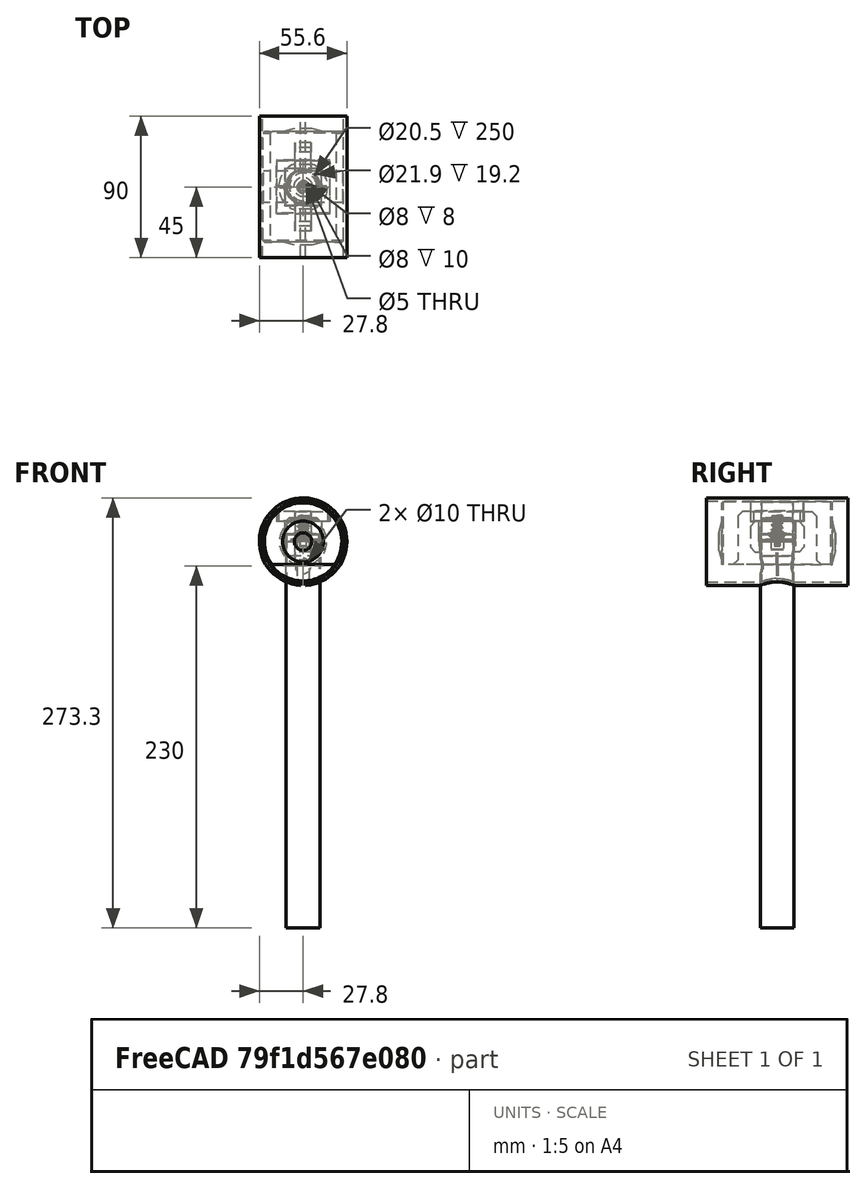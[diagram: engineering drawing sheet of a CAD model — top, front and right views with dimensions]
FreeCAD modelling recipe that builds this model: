
FCSTD DOCUMENT  (FreeCAD 1.0R39109 (Git))
Label: HammerV2
License: All rights reserved
LicenseURL: https://en.wikipedia.org/wiki/All_rights_reserved
objects: TechDraw::DrawViewDimension×61, TechDraw::DrawProjGroupItem×26, Part::Feature×23, Sketcher::SketchObject×22, App::DocumentObjectGroupPython×19, App::FeaturePython×16, App::Link×14, PartDesign::Body×11, TechDraw::DrawViewBalloon×11, PartDesign::Pad×10, PartDesign::Pocket×9, TechDraw::DrawSVGTemplate×9, TechDraw::DrawPage×9, TechDraw::DrawViewAnnotation×8, TechDraw::DrawProjGroup×8, PartDesign::Chamfer×5, App::DocumentObjectGroup×4, PartDesign::PolarPattern×3, PartDesign::Mirrored×3, PartDesign::AdditiveHelix×3, +9 more types
note: 282 computed .brp shape members not serialized (recipe doc carries the construction recipe); baked Part::Feature solids carry a one-line shape summary decoded from their .brp

FEATURE [Sketcher::SketchObject] Sketch011
  ArcFitTolerance = 1e-06
  AttachmentSupport = -> [XY_Plane009]
  FullyConstrained = true
  MakeInternals = false
  MapMode = 5
  sketch-geometry (5):
    g0: LineSegment StartX=-11.55 StartY=-11.55 StartZ=0 EndX=11.55 EndY=-11.55 EndZ=0
    g1: LineSegment StartX=11.55 StartY=-11.55 StartZ=0 EndX=11.55 EndY=11.55 EndZ=0
    g2: LineSegment StartX=11.55 StartY=11.55 StartZ=0 EndX=-11.55 EndY=11.55 EndZ=0
    g3: LineSegment StartX=-11.55 StartY=11.55 StartZ=0 EndX=-11.55 EndY=-11.55 EndZ=0
    g4: GeomPoint [constr] X=0 Y=0 Z=0
  constraints (12):
    c: Coincident(g0,g1)
    c: Coincident(g1,g2)
    c: Coincident(g2,g3)
    c: Coincident(g3,g0)
    c: Horizontal(g0)
    c: Horizontal(g2)
    c: Vertical(g1)
    c: Vertical(g3)
    c: Symmetric(g2,g0,g4)
    c: Coincident(g4,g-1)
    c: DistanceX(g2,g2) = 23.1
    c: Equal(g1,g2)
FEATURE [PartDesign::Pad] Pad007
  Direction = (0,0,1)
  Length = 5
  Length2 = 10
  Profile = -> Sketch011
  ReferenceAxis = -> Sketch011 [N_Axis]
  Refine = true
  Suppressed = false
  Type = 0
FEATURE [Sketcher::SketchObject] Sketch012
  ArcFitTolerance = 1e-06
  AttachmentSupport = -> [XY_Plane009]
  FullyConstrained = true
  MakeInternals = false
  MapMode = 5
  expr: Constraints[16] = 23.1 / 2
  sketch-geometry (6):
    g0: LineSegment StartX=0 StartY=11.55 StartZ=0 EndX=1.8 EndY=11.55 EndZ=0
    g1: LineSegment StartX=1.8 StartY=11.55 StartZ=0 EndX=1.8 EndY=1.8 EndZ=0
    g2: LineSegment StartX=1.8 StartY=1.8 StartZ=0 EndX=11.55 EndY=1.8 EndZ=0
    g3: LineSegment StartX=11.55 StartY=1.8 StartZ=0 EndX=11.55 EndY=0 EndZ=0
    g4: LineSegment StartX=0 StartY=11.55 StartZ=0 EndX=0 EndY=0 EndZ=0
    g5: LineSegment StartX=0 StartY=0 StartZ=0 EndX=11.55 EndY=0 EndZ=0
  constraints (17):
    c: Horizontal(g0)
    c: Coincident(g0,g1)
    c: Vertical(g1)
    c: Coincident(g1,g2)
    c: Horizontal(g2)
    c: Coincident(g2,g3)
    c: Vertical(g3)
    c: Coincident(g4,g0)
    c: Vertical(g4)
    c: Coincident(g5,g4)
    c: Coincident(g5,g3)
    c: Horizontal(g5)
    c: Coincident(g4,g-1)
    c: DistanceX(g0,g0) = 1.8
    c: Equal(g3,g0)
    c: Equal(g4,g5)
    c: DistanceY(g4,g4) = 11.55
FEATURE [PartDesign::Pad] Pad008
  BaseFeature = -> Pad007
  Direction = (0,0,1)
  Length = 2.8
  Length2 = 10
  Profile = -> Sketch012
  ReferenceAxis = -> Sketch012 [N_Axis]
  Refine = true
  Reversed = true
  Suppressed = false
  Type = 0
FEATURE [PartDesign::PolarPattern] PolarPattern001
  Angle = 360
  Axis = -> Sketch012 [N_Axis]
  BaseFeature = -> Pad008
  Mode = 0
  Occurrences = 4
  Offset = 120
  Originals = -> [Pad008]
  Refine = true
  Suppressed = false
  TransformMode = 0
FEATURE [Sketcher::SketchObject] Sketch013
  ArcFitTolerance = 1e-06
  AttachmentSupport = -> [XY_Plane009]
  FullyConstrained = true
  MakeInternals = false
  MapMode = 5
  sketch-geometry (1):
    g0: Circle CenterX=0 CenterY=0 CenterZ=0 NormalX=0 NormalY=0 NormalZ=1 AngleXU=0 Radius=10.5
  constraints (2):
    c: Coincident(g0,g-1)
    c: Diameter(g0) = 21
FEATURE [PartDesign::Pad] Pad009
  BaseFeature = -> PolarPattern001
  Direction = (0,0,1)
  Length = 9
  Length2 = 10
  Profile = -> Sketch013
  ReferenceAxis = -> Sketch013 [N_Axis]
  Refine = true
  Reversed = true
  Suppressed = false
  TaperAngle = -2
  Type = 0
FEATURE [Sketcher::SketchObject] Sketch014
  ArcFitTolerance = 1e-06
  AttachmentOffset = pos=(0,0,-5) rot=(0,0,1;0rad)
  AttachmentSupport = -> [XY_Plane009]
  FullyConstrained = true
  MakeInternals = false
  MapMode = 5
  Placement = pos=(0,0,-5) rot=(0,0,1;0rad)
  sketch-geometry (1):
    g0: Circle CenterX=0 CenterY=0 CenterZ=0 NormalX=0 NormalY=0 NormalZ=1 AngleXU=0 Radius=4
  constraints (2):
    c: Diameter(g0) = 8
    c: Coincident(g0,g-1)
FEATURE [PartDesign::Pocket] Pocket003
  BaseFeature = -> Pad009
  Direction = (0,0,-1)
  Length = 0
  Length2 = 5
  Profile = -> Sketch014
  ReferenceAxis = -> Sketch014 [N_Axis]
  Refine = true
  Suppressed = false
  Type = 3
  UpToFace = -> Pad009 [Face11]
FEATURE [PartDesign::Chamfer] Chamfer003
  Angle = 45
  Base = -> Pocket003 [Edge6,Edge11,Edge39,Edge37]
  BaseFeature = -> Pocket003
  ChamferType = 0
  FlipDirection = false
  Refine = true
  Size = 1
  Size2 = 1
  SupportTransform = false
  Suppressed = false
  UseAllEdges = false
FEATURE [Sketcher::SketchObject] Sketch015
  ArcFitTolerance = 1e-06
  AttachmentSupport = -> [XZ_Plane010]
  FullyConstrained = true
  MakeInternals = false
  MapMode = 5
  Placement = pos=(0,0,0) rot=(1,0,0;1.5708rad)
  expr: Constraints[13] = 5 / 2
  sketch-geometry (6):
    g0: LineSegment StartX=-4e-16 StartY=0 StartZ=0 EndX=2.5 EndY=0 EndZ=0
    g1: LineSegment StartX=2.5 StartY=0 StartZ=0 EndX=2.5 EndY=2.8 EndZ=0
    g2: LineSegment StartX=2.5 StartY=2.8 StartZ=0 EndX=4 EndY=2.8 EndZ=0
    g3: LineSegment StartX=4 StartY=2.8 StartZ=0 EndX=4 EndY=4 EndZ=0
    g4: LineSegment StartX=4 StartY=4 StartZ=0 EndX=0 EndY=4 EndZ=0
    g5: LineSegment StartX=0 StartY=4 StartZ=0 EndX=-4e-16 EndY=0 EndZ=0
  constraints (17):
    c: Coincident(g-1,g0)
    c: PointOnObject(g0,g-1)
    c: Coincident(g0,g1)
    c: Vertical(g1)
    c: Coincident(g1,g2)
    c: Horizontal(g2)
    c: Coincident(g2,g3)
    c: Vertical(g3)
    c: Coincident(g3,g4)
    c: PointOnObject(g4,g-2)
    c: Horizontal(g4)
    c: Coincident(g4,g5)
    c: Coincident(g5,g0)
    c: DistanceX(g0,g0) = 2.5
    c: DistanceX(g4,g4) = 4
    c: DistanceY(g3,g3) = 1.2
    c: DistanceY(g5,g5) = 4
FEATURE [PartDesign::Revolution] Revolution
  Angle = 360
  Angle2 = 60
  Axis = (0,2e-16,1)
  Base = (0,0,0)
  Placement = pos=(0,0,0) rot=(1,0,0;1.5708rad)
  Profile = -> Sketch015
  ReferenceAxis = -> Sketch015 [V_Axis]
  Refine = true
  Reversed = true
  Suppressed = false
  Type = 0
FEATURE [PartDesign::Chamfer] Chamfer002
  Angle = 45
  Base = -> Revolution [Edge1]
  BaseFeature = -> Revolution
  ChamferType = 0
  FlipDirection = false
  Placement = pos=(0,0,0) rot=(1,0,0;1.5708rad)
  Refine = true
  Size = 0.5
  Size2 = 1
  SupportTransform = false
  Suppressed = false
  UseAllEdges = false
FEATURE [PartDesign::Body] Body008  label="Spring_Top"
  AllowCompound = false
  Group = -> [Sketch015,Revolution,Chamfer002]
  Origin = -> Origin010
  Tip = -> Chamfer002
FEATURE [Sketcher::SketchObject] Sketch016
  ArcFitTolerance = 1e-06
  AttachmentSupport = -> [XZ_Plane011]
  FullyConstrained = false
  MakeInternals = false
  MapMode = 5
  Placement = pos=(0,0,0) rot=(1,0,0;1.5708rad)
  expr: Constraints[5] = <<HMRProperties>>.head_diameter
  expr: Constraints[9] = <<HMRProperties>>.head_cutoff
  sketch-geometry (4):
    g0: GeomPoint [constr] X=0 Y=-25.6 Z=0
    g1: ArcOfCircle CenterX=0 CenterY=0 CenterZ=0 NormalX=0 NormalY=0 NormalZ=1 AngleXU=0 Radius=25.6 StartAngle=5.6763 EndAngle=10.0317
    g2: LineSegment StartX=21.0286 StartY=-14.6 StartZ=0 EndX=-21.0286 EndY=-14.6 EndZ=0
    g3: ArcOfCircle [constr] CenterX=0 CenterY=0 CenterZ=0 NormalX=0 NormalY=0 NormalZ=1 AngleXU=0 Radius=25.6 StartAngle=3.89407 EndAngle=5.6763
  constraints (10):
    c: PointOnObject(g0,g-2)
    c: Coincident(g1,g-1)
    c: Coincident(g2,g1)
    c: Coincident(g2,g1)
    c: Horizontal(g2)
    c: Diameter(g1) = 51.2
    c: Coincident(g3,g1)
    c: Coincident(g3,g1)
    c: PointOnObject(g0,g3)
    c: DistanceY(g0,g1) = 11
FEATURE [PartDesign::Pad] Pad010
  Direction = (0,-1,2e-16)
  Length = 70
  Length2 = 10
  Midplane = true
  Placement = pos=(0,0,0) rot=(1,0,0;1.5708rad)
  Profile = -> Sketch016
  ReferenceAxis = -> Sketch016 [N_Axis]
  Refine = true
  Suppressed = false
  Type = 0
  expr: Length = <<HMRProperties>>.head_length
FEATURE [Sketcher::SketchObject] Sketch017
  ArcFitTolerance = 1e-06
  AttachmentOffset = pos=(0,0,25.6) rot=(0,0,1;0rad)
  AttachmentSupport = -> [XY_Plane011]
  FullyConstrained = true
  MakeInternals = false
  MapMode = 5
  Placement = pos=(0,0,25.6) rot=(0,0,1;0rad)
  expr: .AttachmentOffset.Base.z = <<HMRProperties>>.head_diameter / 2
  expr: Constraints[9] = <<HMRProperties>>.top_sensor_pocket_size
  sketch-geometry (5):
    g0: LineSegment StartX=-17 StartY=-17 StartZ=0 EndX=17 EndY=-17 EndZ=0
    g1: LineSegment StartX=17 StartY=-17 StartZ=0 EndX=17 EndY=17 EndZ=0
    g2: LineSegment StartX=17 StartY=17 StartZ=0 EndX=-17 EndY=17 EndZ=0
    g3: LineSegment StartX=-17 StartY=17 StartZ=0 EndX=-17 EndY=-17 EndZ=0
    g4: GeomPoint [constr] X=0 Y=0 Z=0
  constraints (12):
    c: Coincident(g0,g1)
    c: Coincident(g1,g2)
    c: Coincident(g2,g3)
    c: Coincident(g3,g0)
    c: Horizontal(g0)
    c: Horizontal(g2)
    c: Vertical(g1)
    c: Vertical(g3)
    c: Symmetric(g2,g0,g4)
    c: Distance(g0,g2) = 34
    c: Coincident(g4,g-1)
    c: Equal(g0,g3)
FEATURE [PartDesign::Pocket] Pocket004
  BaseFeature = -> Pad010
  Direction = (0,0,-1)
  Length = 13
  Length2 = 5
  Placement = pos=(0,0,0) rot=(1,0,0;1.5708rad)
  Profile = -> Sketch017
  ReferenceAxis = -> Sketch017 [N_Axis]
  Refine = true
  Suppressed = false
  Type = 0
  expr: Length = <<HMRProperties>>.top_sensor_pocket_depth
FEATURE [Sketcher::SketchObject] Sketch018
  ArcFitTolerance = 1e-06
  AttachmentOffset = pos=(0,0,12.6) rot=(0,0,1;0rad)
  AttachmentSupport = -> [XY_Plane011]
  FullyConstrained = true
  MakeInternals = false
  MapMode = 5
  Placement = pos=(0,0,12.6) rot=(0,0,1;0rad)
  expr: .AttachmentOffset.Base.z = <<HMRProperties>>.head_diameter / 2 - <<HMRProperties>>.top_sensor_pocket_depth
  expr: Constraints[11] = <<HMRProperties>>.pusher_pocket_size
  sketch-geometry (5):
    g0: LineSegment StartX=-11.75 StartY=-11.75 StartZ=0 EndX=11.75 EndY=-11.75 EndZ=0
    g1: LineSegment StartX=11.75 StartY=-11.75 StartZ=0 EndX=11.75 EndY=11.75 EndZ=0
    g2: LineSegment StartX=11.75 StartY=11.75 StartZ=0 EndX=-11.75 EndY=11.75 EndZ=0
    g3: LineSegment StartX=-11.75 StartY=11.75 StartZ=0 EndX=-11.75 EndY=-11.75 EndZ=0
    g4: GeomPoint [constr] X=0 Y=0 Z=0
  constraints (12):
    c: Coincident(g0,g1)
    c: Coincident(g1,g2)
    c: Coincident(g2,g3)
    c: Coincident(g3,g0)
    c: Horizontal(g0)
    c: Horizontal(g2)
    c: Vertical(g1)
    c: Vertical(g3)
    c: Symmetric(g2,g0,g4)
    c: Coincident(g4,g-1)
    c: Equal(g2,g1)
    c: DistanceX(g2,g2) = 23.5
FEATURE [PartDesign::Pocket] Pocket005
  BaseFeature = -> Pocket004
  Direction = (0,0,-1)
  Length = 8
  Length2 = 5
  Placement = pos=(0,0,0) rot=(1,0,0;1.5708rad)
  Profile = -> Sketch018
  ReferenceAxis = -> Sketch018 [N_Axis]
  Refine = true
  Suppressed = false
  Type = 0
  expr: Length = <<HMRProperties>>.pusher_pocket_depth
FEATURE [Sketcher::SketchObject] Sketch019
  ArcFitTolerance = 1e-06
  AttachmentOffset = pos=(0,0,25.6) rot=(0,0,1;0rad)
  AttachmentSupport = -> [XY_Plane011]
  FullyConstrained = true
  MakeInternals = false
  MapMode = 5
  Placement = pos=(0,0,25.6) rot=(0,0,1;0rad)
  expr: .AttachmentOffset.Base.z = <<HMRProperties>>.head_diameter / 2
  expr: Constraints[1] = <<HMRProperties>>.handle_hole_diameter
  sketch-geometry (1):
    g0: Circle CenterX=0 CenterY=0 CenterZ=0 NormalX=0 NormalY=0 NormalZ=1 AngleXU=0 Radius=10.95
  constraints (2):
    c: Coincident(g0,g-1)
    c: Diameter(g0) = 21.9
FEATURE [PartDesign::Pocket] Pocket006
  BaseFeature = -> Pocket005
  Direction = (0,0,-1)
  Length = 5
  Length2 = 5
  Placement = pos=(0,0,0) rot=(1,0,0;1.5708rad)
  Profile = -> Sketch019
  ReferenceAxis = -> Sketch019 [N_Axis]
  Refine = true
  Suppressed = false
  Type = 1
FEATURE [Sketcher::SketchObject] Sketch020
  ArcFitTolerance = 1e-06
  AttachmentOffset = pos=(0,0,4.6) rot=(0,0,1;0rad)
  AttachmentSupport = -> [XY_Plane011]
  FullyConstrained = true
  MakeInternals = false
  MapMode = 5
  Placement = pos=(0,0,4.6) rot=(0,0,1;0rad)
  expr: .AttachmentOffset.Base.z = <<HMRProperties>>.head_diameter / 2 - <<HMRProperties>>.top_sensor_pocket_depth - <<HMRProperties>>.pusher_pocket_depth
  expr: Constraints[16] = <<HMRProperties>>.pusher_pocket_size / 2
  sketch-geometry (6):
    g0: LineSegment StartX=0 StartY=11.75 StartZ=0 EndX=2 EndY=11.75 EndZ=0
    g1: LineSegment StartX=2 StartY=11.75 StartZ=0 EndX=2 EndY=2 EndZ=0
    g2: LineSegment StartX=2 StartY=2 StartZ=0 EndX=11.75 EndY=2 EndZ=0
    g3: LineSegment StartX=11.75 StartY=2 StartZ=0 EndX=11.75 EndY=0 EndZ=0
    g4: LineSegment StartX=11.75 StartY=0 StartZ=0 EndX=0 EndY=0 EndZ=0
    g5: LineSegment StartX=0 StartY=0 StartZ=0 EndX=0 EndY=11.75 EndZ=0
  constraints (17):
    c: Horizontal(g0)
    c: Coincident(g0,g1)
    c: Vertical(g1)
    c: Coincident(g1,g2)
    c: Horizontal(g2)
    c: Coincident(g2,g3)
    c: PointOnObject(g3,g-1)
    c: Vertical(g3)
    c: Coincident(g3,g4)
    c: Coincident(g4,g-1)
    c: Coincident(g4,g5)
    c: Coincident(g5,g0)
    c: Vertical(g5)
    c: Equal(g0,g3)
    c: DistanceX(g0,g0) = 2
    c: Equal(g4,g5)
    c: DistanceX(g4,g4) = 11.75
FEATURE [PartDesign::Pocket] Pocket007
  BaseFeature = -> Pocket006
  Direction = (0,0,-1)
  Length = 3
  Length2 = 5
  Placement = pos=(0,0,0) rot=(1,0,0;1.5708rad)
  Profile = -> Sketch020
  ReferenceAxis = -> Sketch020 [N_Axis]
  Refine = true
  Suppressed = false
  Type = 0
  expr: Length = <<HMRProperties>>.pusher_notch_pocket_depth
FEATURE [PartDesign::PolarPattern] PolarPattern002
  Angle = 360
  Axis = -> Sketch020 [N_Axis]
  BaseFeature = -> Pocket007
  Mode = 0
  Occurrences = 4
  Offset = 120
  Originals = -> [Pocket007]
  Placement = pos=(0,0,0) rot=(1,0,0;1.5708rad)
  Refine = true
  Suppressed = false
  TransformMode = 0
FEATURE [Sketcher::SketchObject] Sketch021
  ArcFitTolerance = 1e-06
  AttachmentSupport = -> [YZ_Plane011]
  ExternalGeometry = -> [PolarPattern002]
  FullyConstrained = true
  MakeInternals = false
  MapMode = 5
  Placement = pos=(0,0,0) rot=(0.57735,0.57735,0.57735;2.0944rad)
  sketch-geometry (7):
    g0: LineSegment StartX=-17 StartY=19.1405 StartZ=0 EndX=-17 EndY=-6.6 EndZ=0
    g1: LineSegment StartX=-17 StartY=19.1405 StartZ=0 EndX=-25 EndY=19.1405 EndZ=0
    g2: LineSegment StartX=-25 StartY=19.1405 StartZ=0 EndX=-25 EndY=-14.6 EndZ=0
    g3: LineSegment StartX=-17 StartY=-6.6 StartZ=0 EndX=0 EndY=-6.6 EndZ=0
    g4: LineSegment StartX=0 StartY=-6.6 StartZ=0 EndX=0 EndY=-14.6 EndZ=0
    g5: LineSegment StartX=0 StartY=-14.6 StartZ=0 EndX=-25 EndY=-14.6 EndZ=0
    g6: LineSegment [constr] StartX=-17 StartY=25.6 StartZ=0 EndX=-17 EndY=19.1405 EndZ=0
  constraints (19):
    c: Vertical(g0)
    c: Coincident(g0,g1)
    c: Horizontal(g1)
    c: Coincident(g1,g2)
    c: Vertical(g2)
    c: Coincident(g0,g3)
    c: Coincident(g3,g4)
    c: Vertical(g4)
    c: Coincident(g4,g5)
    c: Coincident(g5,g2)
    c: Horizontal(g5)
    c: Coincident(g6,g-3)
    c: Coincident(g6,g-3)
    c: DistanceX(g1,g1) = 8
    c: Vertical(g-1,g3)
    c: Horizontal(g3)
    c: PointOnObject(g-4,g5)
    c: DistanceY(g2,g0) = 8
    c: Coincident(g0,g6)
FEATURE [PartDesign::Pocket] Pocket008
  BaseFeature = -> PolarPattern002
  Direction = (-1,0,0)
  Length = 10
  Length2 = 5
  Midplane = true
  Placement = pos=(0,0,0) rot=(1,0,0;1.5708rad)
  Profile = -> Sketch021
  ReferenceAxis = -> Sketch021 [N_Axis]
  Refine = true
  Suppressed = false
  Type = 0
  expr: Length = <<HMRProperties>>.wire_width
FEATURE [PartDesign::Mirrored] Mirrored001
  BaseFeature = -> Pocket008
  MirrorPlane = -> Sketch021 [V_Axis]
  Originals = -> [Pocket008]
  Placement = pos=(0,0,0) rot=(1,0,0;1.5708rad)
  Refine = true
  Suppressed = false
  TransformMode = 0
FEATURE [PartDesign::AdditiveCylinder] Cylinder001
  Angle = 360
  AttacherType = Attacher::AttachEngine3D
  AttachmentOffset = pos=(0,0,35) rot=(0,0,1;0rad)
  AttachmentSupport = -> [XZ_Plane011]
  BaseFeature = -> Mirrored001
  FirstAngle = 0
  Height = 2
  MapMode = 5
  Placement = pos=(0,-35,7.8e-15) rot=(1,0,0;1.5708rad)
  Radius = 13
  Refine = true
  SecondAngle = 0
  Suppressed = false
  expr: .AttachmentOffset.Base.z = <<HMRProperties>>.head_length / 2
FEATURE [PartDesign::Draft] Draft
  Angle = 75
  Base = -> Cylinder001 [Face16]
  BaseFeature = -> Cylinder001
  NeutralPlane = -> Cylinder001 [Face4]
  Placement = pos=(0,-35,7.8e-15) rot=(1,0,0;1.5708rad)
  Refine = true
  Reversed = true
  SupportTransform = false
  Suppressed = false
FEATURE [PartDesign::Mirrored] Mirrored002
  BaseFeature = -> Draft
  MirrorPlane = -> XZ_Plane011
  Originals = -> [Cylinder001,Draft]
  Placement = pos=(0,-35,7.8e-15) rot=(1,0,0;1.5708rad)
  Refine = true
  Suppressed = false
  TransformMode = 0
FEATURE [PartDesign::Chamfer] Chamfer004
  Angle = 45
  Base = -> Mirrored002 [Edge80,Edge132,Edge18,Edge90]
  BaseFeature = -> Mirrored002
  ChamferType = 0
  FlipDirection = false
  Placement = pos=(0,-35,7.8e-15) rot=(1,0,0;1.5708rad)
  Refine = true
  Size = 3
  Size2 = 1
  SupportTransform = false
  Suppressed = false
  UseAllEdges = false
FEATURE [PartDesign::Mirrored] Mirrored003
  BaseFeature = -> Chamfer004
  MirrorPlane = -> XZ_Plane011
  Originals = -> [Chamfer004]
  Placement = pos=(0,-35,7.8e-15) rot=(1,0,0;1.5708rad)
  Refine = true
  Suppressed = false
  TransformMode = 0
FEATURE [PartDesign::Chamfer] Chamfer005
  Angle = 45
  Base = -> Mirrored003 [Edge14,Edge15]
  BaseFeature = -> Mirrored003
  ChamferType = 0
  FlipDirection = false
  Placement = pos=(0,-35,7.8e-15) rot=(1,0,0;1.5708rad)
  Refine = true
  Size = 1
  Size2 = 1
  SupportTransform = false
  Suppressed = false
  UseAllEdges = false
FEATURE [PartDesign::Body] Body009  label="Head"
  AllowCompound = false
  Group = -> [Sketch016,Pad010,Sketch017,Pocket004,Sketch018,Pocket005,Sketch019,Pocket006,Sketch020,Pocket007,PolarPattern002,Sketch021,Pocket008,Mirrored001,Cylinder001,Draft,Mirrored002,Chamfer004,Mirrored003,Chamfer005]
  Origin = -> Origin011
  Tip = -> Chamfer005
FEATURE [Sketcher::SketchObject] Sketch022
  ArcFitTolerance = 1e-06
  AttachmentSupport = -> [XZ_Plane012]
  FullyConstrained = true
  MakeInternals = false
  MapMode = 5
  Placement = pos=(0,0,0) rot=(1,0,0;1.5708rad)
  expr: Constraints[35] = 90 - <<HMRProperties>>.plug_draft
  expr: Constraints[4] = <<HMRProperties>>.plug_start_diameter / 2
  expr: Constraints[5] = <<HMRProperties>>.plug_hole_diameter / 2
  expr: Constraints[6] = <<HMRProperties>>.plug_height
  sketch-geometry (16):
    g0: LineSegment StartX=2.5 StartY=13.5858 StartZ=0 EndX=2.5 EndY=1.41421 EndZ=0
    g1: LineSegment StartX=3.91421 StartY=4e-16 StartZ=0 EndX=9.73262 EndY=4e-16 EndZ=0
    g2: LineSegment StartX=11.0966 StartY=1.46271 StartZ=0 EndX=10.2454 EndY=13.636 EndZ=0
    g3: LineSegment StartX=8.78267 StartY=15 StartZ=0 EndX=3.91421 EndY=15 EndZ=0
    g4: ArcOfCircle [constr] CenterX=8.78267 CenterY=13.5337 CenterZ=0 NormalX=0 NormalY=0 NormalZ=1 AngleXU=0 Radius=1.46628 StartAngle=0.0698132 EndAngle=1.5708
    g5: GeomPoint [constr] X=10.15 Y=15 Z=0
    g6: LineSegment StartX=10.2454 StartY=13.636 StartZ=0 EndX=8.78267 EndY=15 EndZ=0
    g7: ArcOfCircle [constr] CenterX=3.91421 CenterY=13.5858 CenterZ=0 NormalX=0 NormalY=0 NormalZ=1 AngleXU=0 Radius=1.41421 StartAngle=1.5708 EndAngle=3.14159
    g8: GeomPoint [constr] X=2.5 Y=15 Z=0
    g9: LineSegment StartX=3.91421 StartY=15 StartZ=0 EndX=2.5 EndY=13.5858 EndZ=0
    g10: ArcOfCircle [constr] CenterX=9.73262 CenterY=1.36733 CenterZ=0 NormalX=0 NormalY=0 NormalZ=1 AngleXU=0 Radius=1.36733 StartAngle=4.71239 EndAngle=6.353
    g11: GeomPoint [constr] X=11.1989 Y=0 Z=0
    g12: LineSegment StartX=9.73262 StartY=4e-16 StartZ=0 EndX=11.0966 EndY=1.46271 EndZ=0
    g13: ArcOfCircle [constr] CenterX=3.91421 CenterY=1.41421 CenterZ=0 NormalX=0 NormalY=0 NormalZ=1 AngleXU=0 Radius=1.41421 StartAngle=3.14159 EndAngle=4.71239
    g14: GeomPoint [constr] X=2.5 Y=0 Z=0
    g15: LineSegment StartX=2.5 StartY=1.41421 StartZ=0 EndX=3.91421 EndY=4e-16 EndZ=0
  constraints (36):
    c: Vertical(g0)
    c: PointOnObject(g11,g-1)
    c: Horizontal(g1)
    c: Horizontal(g3)
    c: DistanceX(g-1,g5) = 10.15
    c: DistanceX(g-1,g14) = 2.5
    c: DistanceY(g14,g8) = 15
    c: PointOnObject(g5,g2)
    c: PointOnObject(g5,g3)
    c: Tangent(g2,g4) = -1.5708
    c: Tangent(g3,g4) = -1.5708
    c: Coincident(g6,g2)
    c: Coincident(g6,g3)
    c: Distance(g6) = 2
    c: PointOnObject(g8,g0)
    c: PointOnObject(g8,g3)
    c: Tangent(g0,g7) = -1.5708
    c: Tangent(g3,g7) = -1.5708
    c: Coincident(g9,g0)
    c: Coincident(g9,g3)
    c: PointOnObject(g11,g1)
    c: PointOnObject(g11,g2)
    c: Tangent(g1,g10) = -1.5708
    c: Tangent(g2,g10) = -1.5708
    c: Coincident(g12,g1)
    c: Coincident(g12,g2)
    c: PointOnObject(g14,g0)
    c: PointOnObject(g14,g1)
    c: Tangent(g0,g13) = -1.5708
    c: Tangent(g1,g13) = -1.5708
    c: Coincident(g15,g0)
    c: Coincident(g15,g1)
    c: Equal(g15,g12)
    c: Equal(g6,g9)
    c: Equal(g9,g15)
    c: Angle(g2,g1) = 1.50098
FEATURE [PartDesign::Revolution] Revolution001
  Angle = 360
  Angle2 = 60
  Axis = (0,2e-16,1)
  Base = (0,0,0)
  Placement = pos=(0,0,0) rot=(1,0,0;1.5708rad)
  Profile = -> Sketch022
  ReferenceAxis = -> Sketch022 [V_Axis]
  Refine = true
  Reversed = true
  Suppressed = false
  Type = 0
FEATURE [PartDesign::Body] Body010  label="Plug"
  AllowCompound = false
  Group = -> [Sketch022,Revolution001]
  Origin = -> Origin012
  Tip = -> Revolution001
FEATURE [Sketcher::SketchObject] Sketch023
  ArcFitTolerance = 1e-06
  AttachmentSupport = -> [XY_Plane013]
  FullyConstrained = true
  MakeInternals = false
  MapMode = 5
  expr: Constraints[2] = <<HMRProperties>>.Handle_ID
  expr: Constraints[3] = <<HMRProperties>>.Handle_OD
  sketch-geometry (2):
    g0: Circle CenterX=0 CenterY=0 CenterZ=0 NormalX=0 NormalY=0 NormalZ=1 AngleXU=0 Radius=10.75
    g1: Circle CenterX=0 CenterY=0 CenterZ=0 NormalX=0 NormalY=0 NormalZ=1 AngleXU=0 Radius=10.25
  constraints (4):
    c: Coincident(g0,g-1)
    c: Coincident(g1,g0)
    c: Diameter(g1) = 20.5
    c: Diameter(g0) = 21.5
FEATURE [PartDesign::Pad] Pad011
  Direction = (0,0,1)
  Length = 250
  Length2 = 10
  Profile = -> Sketch023
  ReferenceAxis = -> Sketch023 [N_Axis]
  Refine = true
  Reversed = true
  Suppressed = false
  Type = 0
FEATURE [Sketcher::SketchObject] Sketch024
  ArcFitTolerance = 1e-06
  AttachmentSupport = -> [XY_Plane013]
  FullyConstrained = true
  MakeInternals = false
  MapMode = 5
  sketch-geometry (6):
    g0: LineSegment StartX=0 StartY=12.14 StartZ=0 EndX=2 EndY=12.14 EndZ=0
    g1: LineSegment StartX=2 StartY=12.14 StartZ=0 EndX=2 EndY=2 EndZ=0
    g2: LineSegment StartX=2 StartY=2 StartZ=0 EndX=12.14 EndY=2 EndZ=0
    g3: LineSegment StartX=12.14 StartY=2 StartZ=0 EndX=12.14 EndY=0 EndZ=0
    g4: LineSegment StartX=12.14 StartY=0 StartZ=0 EndX=0 EndY=0 EndZ=0
    g5: LineSegment StartX=0 StartY=0 StartZ=0 EndX=0 EndY=12.14 EndZ=0
  constraints (17):
    c: Coincident(g0,g1)
    c: Vertical(g1)
    c: Coincident(g1,g2)
    c: Horizontal(g2)
    c: Coincident(g2,g3)
    c: Vertical(g3)
    c: Coincident(g3,g4)
    c: Coincident(g4,g5)
    c: Coincident(g5,g0)
    c: Horizontal(g4)
    c: Vertical(g5)
    c: Horizontal(g0)
    c: Coincident(g4,g-1)
    c: Equal(g2,g1)
    c: Equal(g0,g3)
    c: DistanceX(g4,g4) = 12.14
    c: DistanceY(g3,g3) = 2
FEATURE [PartDesign::Pocket] Pocket009
  BaseFeature = -> Pad011
  Direction = (0,0,-1)
  Length = 3
  Length2 = 5
  Profile = -> Sketch024
  ReferenceAxis = -> Sketch024 [N_Axis]
  Refine = true
  Suppressed = false
  Type = 0
FEATURE [PartDesign::PolarPattern] PolarPattern003
  Angle = 360
  Axis = -> Z_Axis013
  BaseFeature = -> Pocket009
  Mode = 0
  Occurrences = 4
  Offset = 120
  Originals = -> [Pocket009]
  Refine = true
  Suppressed = false
  TransformMode = 0
FEATURE [PartDesign::SubtractiveCylinder] Cylinder002
  Angle = 360
  AttacherType = Attacher::AttachEngine3D
  AttachmentOffset = pos=(0,-20,-12) rot=(0,0,1;0rad)
  AttachmentSupport = -> [XZ_Plane013]
  BaseFeature = -> PolarPattern003
  FirstAngle = 0
  Height = 24
  MapMode = 2
  Placement = pos=(0,12,-20) rot=(1,0,0;1.5708rad)
  Radius = 5
  Refine = true
  SecondAngle = 0
  Suppressed = false
  expr: Radius = <<HMRProperties>>.wire_width / 2
FEATURE [PartDesign::Body] Body011  label="Handle"
  AllowCompound = false
  Group = -> [Sketch023,Pad011,Sketch024,Pocket009,PolarPattern003,Cylinder002]
  Origin = -> Origin013
  Placement = pos=(0,0,4.5) rot=(0,0,1;0rad)
  Tip = -> Cylinder002
FEATURE [Sketcher::SketchObject] Sketch025
  ArcFitTolerance = 1e-06
  AttachmentSupport = -> [XZ_Plane014]
  FullyConstrained = true
  MakeInternals = false
  MapMode = 5
  Placement = pos=(0,0,0) rot=(1,0,0;1.5708rad)
  expr: Constraints[16] = <<HMRProperties>>.top_sensor_holder_height
  expr: Constraints[17] = <<HMRProperties>>.top_sensor_holder_size
  expr: Constraints[1] = <<HMRProperties>>.head_diameter
  sketch-geometry (7):
    g0: Circle [constr] CenterX=0 CenterY=0 CenterZ=0 NormalX=0 NormalY=0 NormalZ=1 AngleXU=0 Radius=25.6
    g1: ArcOfCircle CenterX=0 CenterY=0 CenterZ=0 NormalX=0 NormalY=0 NormalZ=1 AngleXU=0 Radius=25.6 StartAngle=0.854958 EndAngle=2.28663
    g2: LineSegment StartX=-16.8 StartY=19.3163 StartZ=0 EndX=-16.8 EndY=13 EndZ=0
    g3: LineSegment StartX=-16.8 StartY=13 StartZ=0 EndX=16.8 EndY=13 EndZ=0
    g4: LineSegment StartX=16.8 StartY=13 StartZ=0 EndX=16.8 EndY=19.3163 EndZ=0
    g5: LineSegment [constr] StartX=-5 StartY=25.6 StartZ=0 EndX=5 EndY=25.6 EndZ=0
    g6: GeomPoint [constr] X=4e-16 Y=25.6 Z=0
  constraints (18):
    c: Coincident(g0,g-1)
    c: Diameter(g0) = 51.2
    c: Coincident(g1,g0)
    c: PointOnObject(g1,g0)
    c: Coincident(g2,g1)
    c: Vertical(g2)
    c: Coincident(g3,g2)
    c: Horizontal(g3)
    c: Coincident(g4,g3)
    c: Coincident(g4,g1)
    c: Vertical(g4)
    c: Horizontal(g1,g1)
    c: Tangent(g5,g0)
    c: Symmetric(g5,g5,g-2)
    c: DistanceX(g5,g5) = 10
    c: Symmetric(g5,g5,g6)
    c: DistanceY(g3,g6) = 12.6
    c: DistanceX(g3,g3) = 33.6
FEATURE [PartDesign::Pad] Pad012
  Direction = (0,-1,2e-16)
  Length = 33.6
  Length2 = 10
  Midplane = true
  Placement = pos=(0,0,0) rot=(1,0,0;1.5708rad)
  Profile = -> Sketch025
  ReferenceAxis = -> Sketch025 [N_Axis]
  Refine = true
  Suppressed = false
  Type = 0
  expr: Length = <<HMRProperties>>.top_sensor_holder_size
FEATURE [Sketcher::SketchObject] Sketch026
  ArcFitTolerance = 1e-06
  AttachmentSupport = -> [XY_Plane014]
  FullyConstrained = true
  MakeInternals = false
  MapMode = 5
  expr: Constraints[11] = <<HMRProperties>>.top_sensor_holder_size
  expr: Constraints[31] = <<HMRProperties>>.Sensor_Diameter + 1
  expr: Constraints[32] = <<HMRProperties>>.wire_width
  sketch-geometry (13):
    g0: LineSegment [constr] StartX=-16.8 StartY=-16.8 StartZ=0 EndX=16.8 EndY=-16.8 EndZ=0
    g1: LineSegment [constr] StartX=16.8 StartY=-16.8 StartZ=0 EndX=16.8 EndY=16.8 EndZ=0
    g2: LineSegment [constr] StartX=16.8 StartY=16.8 StartZ=0 EndX=-16.8 EndY=16.8 EndZ=0
    g3: LineSegment [constr] StartX=-16.8 StartY=16.8 StartZ=0 EndX=-16.8 EndY=-16.8 EndZ=0
    g4: GeomPoint [constr] X=0 Y=0 Z=0
    g5: ArcOfCircle CenterX=0 CenterY=0 CenterZ=0 NormalX=0 NormalY=0 NormalZ=1 AngleXU=0 Radius=15.5 StartAngle=5.04084 EndAngle=7.52553
    g6: ArcOfCircle CenterX=0 CenterY=0 CenterZ=0 NormalX=0 NormalY=0 NormalZ=1 AngleXU=0 Radius=15.5 StartAngle=1.89925 EndAngle=4.38393
    g7: LineSegment StartX=-5 StartY=14.6714 StartZ=0 EndX=-5 EndY=16.8 EndZ=0
    g8: LineSegment StartX=-5 StartY=16.8 StartZ=0 EndX=5 EndY=16.8 EndZ=0
    g9: LineSegment StartX=5 StartY=16.8 StartZ=0 EndX=5 EndY=14.6714 EndZ=0
    g10: LineSegment StartX=5 StartY=-14.6714 StartZ=0 EndX=5 EndY=-16.8 EndZ=0
    g11: LineSegment StartX=5 StartY=-16.8 StartZ=0 EndX=-5 EndY=-16.8 EndZ=0
    g12: LineSegment StartX=-5 StartY=-16.8 StartZ=0 EndX=-5 EndY=-14.6714 EndZ=0
  constraints (35):
    c: Coincident(g0,g1)
    c: Coincident(g1,g2)
    c: Coincident(g2,g3)
    c: Coincident(g3,g0)
    c: Horizontal(g0)
    c: Horizontal(g2)
    c: Vertical(g1)
    c: Vertical(g3)
    c: Symmetric(g2,g0,g4)
    c: Coincident(g4,g-1)
    c: Equal(g2,g1)
    c: DistanceX(g2,g2) = 33.6
    c: Coincident(g5,g4)
    c: Coincident(g6,g4)
    c: Coincident(g7,g6)
    c: PointOnObject(g7,g2)
    c: Vertical(g7)
    c: Coincident(g8,g7)
    c: Coincident(g9,g8)
    c: PointOnObject(g10,g0)
    c: Vertical(g10)
    c: Coincident(g11,g10)
    c: PointOnObject(g11,g0)
    c: Coincident(g12,g11)
    c: Coincident(g12,g6)
    c: Vertical(g12)
    c: Vertical(g9)
    c: Coincident(g5,g9)
    c: Coincident(g5,g10)
    c: Horizontal(g5,g6)
    c: Horizontal(g5,g6)
    c: Diameter(g5) = 31
    c: DistanceX(g8,g8) = 10
    c: Symmetric(g8,g7,g-2)
    c: Equal(g11,g8)
FEATURE [PartDesign::Pocket] Pocket010
  BaseFeature = -> Pad012
  Direction = (0,0,-1)
  Length = 0
  Length2 = 5
  Offset = 6
  Placement = pos=(0,0,0) rot=(1,0,0;1.5708rad)
  Profile = -> Sketch026
  ReferenceAxis = -> Sketch026 [N_Axis]
  Refine = true
  Suppressed = false
  Type = 3
  UpToFace = -> Pad012 [Face3]
FEATURE [PartDesign::Body] Body012  label="Head_Top"
  AllowCompound = false
  Group = -> [Sketch025,Pad012,Sketch026,Pocket010]
  Origin = -> Origin014
  Tip = -> Pocket010
FEATURE [Sketcher::SketchObject] Sketch032
  ArcFitTolerance = 1e-06
  AttachmentSupport = -> [XZ_Plane017]
  FullyConstrained = true
  MakeInternals = false
  MapMode = 5
  Placement = pos=(0,0,0) rot=(1,0,0;1.5708rad)
  expr: Constraints[1] = <<HMRProperties>>.head_diameter + <<HMRProperties>>.Clearance * 2
  sketch-geometry (2):
    g0: Circle CenterX=0 CenterY=0 CenterZ=0 NormalX=0 NormalY=0 NormalZ=1 AngleXU=0 Radius=25.8
    g1: Circle CenterX=0 CenterY=0 CenterZ=0 NormalX=0 NormalY=0 NormalZ=1 AngleXU=0 Radius=27.8
  constraints (4):
    c: Coincident(g0,g-1)
    c: Diameter(g0) = 51.6
    c: Diameter(g1) = 55.6
    c: Coincident(g1,g0)
FEATURE [PartDesign::Pad] Pad016
  Direction = (0,-1,2e-16)
  Length = 90
  Length2 = 10
  Midplane = true
  Placement = pos=(0,0,0) rot=(1,0,0;1.5708rad)
  Profile = -> Sketch032
  ReferenceAxis = -> Sketch032 [N_Axis]
  Refine = true
  Suppressed = false
  Type = 0
  expr: Length = 90
FEATURE [Sketcher::SketchObject] Sketch033
  ArcFitTolerance = 1e-06
  AttachmentSupport = -> [XY_Plane017]
  FullyConstrained = true
  MakeInternals = false
  MapMode = 5
  expr: Constraints[13] = <<HMRProperties>>.Handle_OD
  sketch-geometry (8):
    g0: LineSegment StartX=1.5 StartY=10.6448 StartZ=0 EndX=1.5 EndY=45 EndZ=0
    g1: LineSegment StartX=-1.5 StartY=10.6448 StartZ=0 EndX=-1.5 EndY=45 EndZ=0
    g2: LineSegment StartX=-1.5 StartY=-10.6448 StartZ=0 EndX=-1.5 EndY=-45 EndZ=0
    g3: LineSegment StartX=1.5 StartY=-45 StartZ=0 EndX=1.5 EndY=-10.6448 EndZ=0
    g4: ArcOfCircle CenterX=0 CenterY=0 CenterZ=0 NormalX=0 NormalY=0 NormalZ=1 AngleXU=0 Radius=10.75 StartAngle=4.85238 EndAngle=7.71399
    g5: ArcOfCircle CenterX=0 CenterY=0 CenterZ=0 NormalX=0 NormalY=0 NormalZ=1 AngleXU=0 Radius=10.75 StartAngle=1.71079 EndAngle=4.5724
    g6: LineSegment StartX=1.5 StartY=-45 StartZ=0 EndX=-1.5 EndY=-45 EndZ=0
    g7: LineSegment StartX=-1.5 StartY=45 StartZ=0 EndX=1.5 EndY=45 EndZ=0
  constraints (23):
    c: Vertical(g0)
    c: Vertical(g1)
    c: Vertical(g2)
    c: Vertical(g3)
    c: Horizontal(g3,g2)
    c: Horizontal(g0,g1)
    c: Equal(g0,g3)
    c: DistanceY(g3,g0) = 90
    c: Coincident(g4,g-1)
    c: Coincident(g4,g0)
    c: Coincident(g4,g3)
    c: Coincident(g5,g4)
    c: Coincident(g5,g2)
    c: Diameter(g4) = 21.5
    c: Coincident(g5,g1)
    c: Coincident(g6,g3)
    c: Coincident(g6,g2)
    c: Symmetric(g3,g2,g-2)
    c: DistanceX(g6,g6) = 3
    c: Coincident(g7,g1)
    c: Coincident(g7,g0)
    c: Horizontal(g7)
    c: Equal(g7,g6)
FEATURE [PartDesign::Pocket] Pocket013
  BaseFeature = -> Pad016
  Direction = (0,0,-1)
  Length = 5
  Length2 = 5
  Placement = pos=(0,0,0) rot=(1,0,0;1.5708rad)
  Profile = -> Sketch033
  ReferenceAxis = -> Sketch033 [N_Axis]
  Refine = true
  Suppressed = false
  Type = 1
FEATURE [PartDesign::Body] Body015  label="Shell"
  AllowCompound = false
  Group = -> [Sketch032,Pad016,Sketch033,Pocket013]
  Origin = -> Origin017
  Tip = -> Pocket013
FEATURE [Sketcher::SketchObject] Sketch034
  ArcFitTolerance = 1e-06
  AttachmentSupport = -> [XZ_Plane018]
  FullyConstrained = true
  MakeInternals = false
  MapMode = 5
  Placement = pos=(0,0,0) rot=(1,0,0;1.5708rad)
  sketch-geometry (1):
    g0: Circle CenterX=0 CenterY=0 CenterZ=0 NormalX=0 NormalY=0 NormalZ=1 AngleXU=0 Radius=25
  constraints (2):
    c: Coincident(g0,g-1)
    c: Diameter(g0) = 50
FEATURE [PartDesign::Pad] Pad017
  Direction = (0,-1,2e-16)
  Length = 20
  Length2 = 10
  Midplane = true
  Placement = pos=(0,0,0) rot=(1,0,0;1.5708rad)
  Profile = -> Sketch034
  ReferenceAxis = -> Sketch034 [N_Axis]
  Refine = true
  Suppressed = false
  Type = 0
FEATURE [PartDesign::Body] Body016  label="FoamL"
  AllowCompound = false
  Group = -> [Sketch034,Pad017]
  Origin = -> Origin018
  Tip = -> Pad017
FEATURE [Sketcher::SketchObject] Sketch035
  ArcFitTolerance = 1e-06
  AttachmentSupport = -> [XY_Plane019]
  FullyConstrained = true
  MakeInternals = false
  MapMode = 5
  sketch-geometry (1):
    g0: Circle CenterX=0 CenterY=0 CenterZ=0 NormalX=0 NormalY=0 NormalZ=1 AngleXU=0 Radius=4
  constraints (2):
    c: Diameter(g0) = 8
    c: Coincident(g0,g-1)
FEATURE [PartDesign::Pad] Pad018
  Direction = (0,0,1)
  Length = 6
  Length2 = 10
  Profile = -> Sketch035
  ReferenceAxis = -> Sketch035 [N_Axis]
  Refine = true
  Suppressed = false
  Type = 0
FEATURE [PartDesign::Body] Body017  label="FoamS"
  AllowCompound = false
  Group = -> [Sketch035,Pad018]
  Origin = -> Origin019
  Tip = -> Pad018
FEATURE [Sketcher::SketchObject] Sketch036
  ArcFitTolerance = 1e-06
  AttachmentSupport = -> [XZ_Plane020]
  FullyConstrained = true
  MakeInternals = false
  MapMode = 5
  Placement = pos=(0,0,0) rot=(1,0,0;1.5708rad)
  sketch-geometry (4):
    g0: ArcOfCircle CenterX=0 CenterY=0 CenterZ=0 NormalX=0 NormalY=0 NormalZ=1 AngleXU=0 Radius=15 StartAngle=4.98232 EndAngle=10.7256
    g1: LineSegment StartX=-4 StartY=-14.4568 StartZ=0 EndX=-4 EndY=-24.4568 EndZ=0
    g2: LineSegment StartX=-4 StartY=-24.4568 StartZ=0 EndX=4 EndY=-24.4568 EndZ=0
    g3: LineSegment StartX=4 StartY=-24.4568 StartZ=0 EndX=4 EndY=-14.4568 EndZ=0
  constraints (11):
    c: Coincident(g0,g-1)
    c: Coincident(g1,g0)
    c: Vertical(g1)
    c: Coincident(g2,g1)
    c: Coincident(g3,g2)
    c: Coincident(g3,g0)
    c: Vertical(g3)
    c: Symmetric(g2,g1,g-2)
    c: DistanceX(g2,g2) = 8
    c: Diameter(g0) = 30
    c: DistanceY(g3,g3) = 10
FEATURE [PartDesign::Pad] Pad019
  Direction = (0,-1,2e-16)
  Length = 1
  Length2 = 10
  Midplane = true
  Placement = pos=(0,0,0) rot=(1,0,0;1.5708rad)
  Profile = -> Sketch036
  ReferenceAxis = -> Sketch036 [N_Axis]
  Refine = true
  Suppressed = false
  Type = 0
FEATURE [PartDesign::Body] Body018  label="Sensor"
  AllowCompound = false
  Group = -> [Sketch036,Pad019]
  Origin = -> Origin020
  Tip = -> Pad019
FEATURE [Spreadsheet::Sheet] Spreadsheet002  label="HMRProperties"
  cells = A1='PropertyName; B1='Value; A2='Clearance; B2(Clearance)=0.2; A3='Handle_OD; B3(Handle_OD)=21.5; A4='shell_ID; B4(shell_ID)=51.4; A5='shell_length; B5(shell_length)=110; A6='head_diameter; B6(head_diameter)==shell_ID - Clearance; C6='calculated; A7='head_length; B7(head_length)=70; A8='wire_width; B8(wire_width)=10; A9='Sensor_Diameter; B9(Sensor_Diameter)=30; A10='Handle_ID; B10(Handle_ID)=20.5; A11='head_cutoff; B11(head_cutoff)=11; A12='top_sensor_pocket_depth; B12(top_sensor_pocket_depth)=13; A13='pusher_pocket_depth; B13(pusher_pocket_depth)=8; A14='pusher_notch_pocket_depth; B14(pusher_notch_pocket_depth)=3; A15='pusher_pocket_size; B15(pusher_pocket_size)=23.5; A16='top_sensor_pocket_size; B16(top_sensor_pocket_size)=34; A17='handle_hole_diameter; B17(handle_hole_diameter)==Handle_OD + Clearance * 2; C17='calculated; A18='plug_hole_diameter; B18(plug_hole_diameter)=5; A19='plug_height; B19(plug_height)=15; A20='plug_draft; B20(plug_draft)=4; A21='plug_start_diameter; B21(plug_start_diameter)==Handle_ID - Clearance; C21='calculated; A22='top_sensor_holder_size; B22(top_sensor_holder_size)==top_sensor_pocket_size - Clearance * 2; C22='calculated; A23='top_sensor_holder_height; B23(top_sensor_holder_height)==top_sensor_pocket_depth - Clearance * 2; C23='calculated; A24='spring_dia; B24(spring_dia)=1
FEATURE [Sketcher::SketchObject] Sketch
  ArcFitTolerance = 1e-06
  AttachmentSupport = -> [XZ_Plane021]
  FullyConstrained = true
  MakeInternals = false
  MapMode = 5
  Placement = pos=(0,0,0) rot=(1,0,0;1.5708rad)
  expr: Constraints[0] = <<HMRProperties>>.spring_dia
  sketch-geometry (1):
    g0: Circle CenterX=3 CenterY=2.2 CenterZ=0 NormalX=0 NormalY=0 NormalZ=1 AngleXU=0 Radius=0.5
  constraints (3):
    c: Diameter(g0) = 1
    c: DistanceX(g-1,g0) = 3
    c: DistanceY(g-1,g0) = 2.2
FEATURE [PartDesign::AdditiveHelix] AdditiveHelix
  Angle = 0
  Axis = (0,2e-16,1)
  Base = (0,0,0)
  Growth = 0
  HasBeenEdited = true
  Height = 13
  LeftHanded = false
  Mode = 0
  Outside = false
  Pitch = 3
  Placement = pos=(0,0,0) rot=(1,0,0;1.5708rad)
  Profile = -> Sketch
  ReferenceAxis = -> Sketch [V_Axis]
  Refine = true
  Suppressed = false
  Tolerance = 0.1
  Turns = 4.33333
FEATURE [PartDesign::AdditiveHelix] AdditiveHelix001
  Angle = 0
  Axis = (1e-16,1e-16,1)
  Base = (0,0,0)
  BaseFeature = -> AdditiveHelix
  Growth = 0
  HasBeenEdited = true
  Height = 1.1
  LeftHanded = false
  Mode = 2
  Outside = false
  Pitch = 1.1
  Placement = pos=(0,0,0) rot=(1,0,0;1.5708rad)
  Profile = -> AdditiveHelix [Edge11]
  ReferenceAxis = -> Z_Axis021
  Refine = true
  Suppressed = false
  Tolerance = 0.1
  Turns = 1
  expr: Height = <<HMRProperties>>.spring_dia + 0.1
FEATURE [TechDraw::DrawViewAnnotation] Annotation004
  Font = osifont
  LineSpace = 100
  LockPosition = false
  MaxWidth = -1
  Rotation = 0
  ScaleType = 0
  Text = A
  TextSize = 4
  TextStyle = 0
  X = 141.15
  Y = 145.557
FEATURE [TechDraw::DrawViewAnnotation] Annotation005
  Font = osifont
  LineSpace = 100
  LockPosition = false
  MaxWidth = -1
  Rotation = 0
  ScaleType = 0
  Text = A
  TextSize = 4
  TextStyle = 0
  X = 141.15
  Y = 89.4917
FEATURE [TechDraw::DrawViewAnnotation] Annotation006
  Font = osifont
  LineSpace = 100
  LockPosition = false
  MaxWidth = -1
  Rotation = 0
  ScaleType = 0
  Text = Changes: | - Cut off a section of the bottom to give room for wires | - Resesign of the top sensor pusher mechanism | after getting good feedback (it now uses a spring) | - Overall design simplifications
  TextSize = 4
  TextStyle = 0
  X = 122.117
  Y = 50.9781
FEATURE [TechDraw::DrawViewAnnotation] Annotation007
  Font = osifont
  LineSpace = 100
  LockPosition = false
  MaxWidth = -1
  Rotation = 0
  Scale = 3
  ScaleType = 0
  Text = Changes: | Has a hole to hold a spring. | Uses a spring to press on the top sensor.
  TextSize = 4
  TextStyle = 0
  X = 205.99
  Y = 77.212
FEATURE [TechDraw::DrawViewAnnotation] Annotation008
  Font = osifont
  LineSpace = 100
  LockPosition = false
  MaxWidth = -1
  Rotation = 0
  ScaleType = 0
  Text = Changes: | Simplified design. Removed unnecessary details.
  TextSize = 4
  TextStyle = 0
  X = 211.362
  Y = 82.9778
FEATURE [TechDraw::DrawProjGroupItem] ProjItem017  label="Top003"
  CoarseView = false
  Direction = (0,0,1)
  Focus = 100
  HardHidden = true
  IsoCount = 0
  IsoHidden = false
  IsoVisible = false
  LockPosition = false
  Perspective = false
  Rotation = 0
  RotationVector = (1,0,0)
  Scale = 3
  ScaleType = 0
  ScrubCount = 1
  SeamHidden = false
  SeamVisible = false
  SmoothHidden = false
  SmoothVisible = true
  Source = -> [Body010]
  Type = 4
  X = 0
  XDirection = (1,0,0)
  Y = 83.7959
FEATURE [TechDraw::DrawViewDimension] Dimension117
  AngleOverride = false
  Arbitrary = false
  ArbitraryTolerances = false
  BoxCorners = (2) [(-33.2899,-33.2899,0),(33.2899,33.2899,0)]
  EqualTolerance = true
  ExtensionAngle = 0
  FormatSpec = ⌀%.2w
  FormatSpecOverTolerance = %+.2w
  FormatSpecUnderTolerance = %+.2w
  Inverted = false
  LineAngle = 0
  LockPosition = false
  MeasureType = 1
  OverTolerance = 0
  References2D = -> [ProjItem017]
  Rotation = 0
  Scale = 3
  ScaleType = 0
  TheoreticalExact = false
  Type = 5
  UnderTolerance = 0
  X = 42.6593
  Y = 21.4032
FEATURE [TechDraw::DrawViewDimension] Dimension118
  AngleOverride = false
  Arbitrary = false
  ArbitraryTolerances = false
  BoxCorners = (2) [(-33.2899,-33.2899,0),(33.2899,33.2899,0)]
  EqualTolerance = true
  ExtensionAngle = 0
  FormatSpec = ⌀%.2w
  FormatSpecOverTolerance = %+.2w
  FormatSpecUnderTolerance = %+.2w
  Inverted = false
  LineAngle = 0
  LockPosition = false
  MeasureType = 1
  OverTolerance = 0
  References2D = -> [ProjItem017]
  Rotation = 0
  Scale = 3
  ScaleType = 0
  TheoreticalExact = false
  Type = 5
  UnderTolerance = 0
  X = 51.3026
  Y = 11.6188
FEATURE [TechDraw::DrawViewDimension] Dimension119
  AngleOverride = false
  Arbitrary = false
  ArbitraryTolerances = false
  BoxCorners = (2) [(-33.2899,-33.2899,0),(33.2899,33.2899,0)]
  EqualTolerance = true
  ExtensionAngle = 0
  FormatSpec = ⌀%.2w
  FormatSpecOverTolerance = %+.2w
  FormatSpecUnderTolerance = %+.2w
  Inverted = false
  LineAngle = 0
  LockPosition = false
  MeasureType = 1
  OverTolerance = 0
  References2D = -> [ProjItem017]
  Rotation = 0
  Scale = 3
  ScaleType = 0
  TheoreticalExact = false
  Type = 5
  UnderTolerance = 0
  X = 49.8742
  Y = -9.48766
FEATURE [TechDraw::DrawProjGroupItem] ProjItem018  label="FrontTopRight006"
  CoarseView = false
  Direction = (0.57735,-0.57735,0.57735)
  Focus = 100
  HardHidden = false
  IsoCount = 0
  IsoHidden = false
  IsoVisible = false
  LockPosition = false
  Perspective = false
  Rotation = 0
  RotationVector = (1,0,0)
  Scale = 3
  ScaleType = 0
  ScrubCount = 1
  SeamHidden = false
  SeamVisible = false
  SmoothHidden = false
  SmoothVisible = true
  Source = -> [Body010]
  Type = 7
  X = 116.826
  XDirection = (0.707107,0.707107,0)
  Y = 81.3881
FEATURE [TechDraw::DrawProjGroupItem] ProjItem022  label="FrontTopRight008"
  CoarseView = false
  Direction = (0.57735,-0.57735,0.57735)
  Focus = 100
  HardHidden = false
  IsoCount = 0
  IsoHidden = false
  IsoVisible = false
  LockPosition = false
  Perspective = false
  Rotation = 0
  RotationVector = (1,0,0)
  Scale = 8
  ScaleType = 0
  ScrubCount = 1
  SeamHidden = false
  SeamVisible = false
  SmoothHidden = false
  SmoothVisible = true
  Source = -> [Body008]
  Type = 7
  X = 115.348
  XDirection = (0.707107,0.707107,0)
  Y = -0.757619
FEATURE [TechDraw::DrawProjGroupItem] ProjItem023  label="Bottom002"
  CoarseView = false
  Direction = (0,0,-1)
  Focus = 100
  HardHidden = true
  IsoCount = 0
  IsoHidden = false
  IsoVisible = false
  LockPosition = false
  Perspective = false
  Rotation = 0
  RotationVector = (1,0,0)
  Scale = 8
  ScaleType = 0
  ScrubCount = 1
  SeamHidden = false
  SeamVisible = false
  SmoothHidden = false
  SmoothVisible = true
  Source = -> [Body008]
  Type = 5
  X = 0
  XDirection = (1,0,0)
  Y = -78.603
FEATURE [TechDraw::DrawViewDimension] Dimension135
  AngleOverride = false
  Arbitrary = false
  ArbitraryTolerances = false
  BoxCorners = (2) [(-32,-32,0),(32,32,0)]
  EqualTolerance = true
  ExtensionAngle = 0
  FormatSpec = ⌀%.2w
  FormatSpecOverTolerance = %+.2w
  FormatSpecUnderTolerance = %+.2w
  Inverted = false
  LineAngle = 0
  LockPosition = false
  MeasureType = 1
  OverTolerance = 0
  References2D = -> [ProjItem023]
  Rotation = 0
  Scale = 8
  ScaleType = 0
  TheoreticalExact = false
  Type = 5
  UnderTolerance = 0
  X = 29.4216
  Y = 32.5739
FEATURE [TechDraw::DrawViewDimension] Dimension136
  AngleOverride = false
  Arbitrary = false
  ArbitraryTolerances = false
  BoxCorners = (2) [(-32,-32,0),(32,32,0)]
  EqualTolerance = true
  ExtensionAngle = 0
  FormatSpec = ⌀%.2w
  FormatSpecOverTolerance = %+.2w
  FormatSpecUnderTolerance = %+.2w
  Inverted = false
  LineAngle = 0
  LockPosition = false
  MeasureType = 1
  OverTolerance = 0
  References2D = -> [ProjItem023]
  Rotation = 0
  Scale = 8
  ScaleType = 0
  TheoreticalExact = false
  Type = 5
  UnderTolerance = 0
  X = 18.5451
  Y = 43.1581
FEATURE [TechDraw::DrawViewDimension] Dimension137
  AngleOverride = false
  Arbitrary = false
  ArbitraryTolerances = false
  BoxCorners = (2) [(-32,-32,0),(32,32,0)]
  EqualTolerance = true
  ExtensionAngle = 0
  FormatSpec = ⌀%.2w
  FormatSpecOverTolerance = %+.2w
  FormatSpecUnderTolerance = %+.2w
  Inverted = false
  LineAngle = 0
  LockPosition = false
  MeasureType = 1
  OverTolerance = 0
  References2D = -> [ProjItem023]
  Rotation = 0
  Scale = 8
  ScaleType = 0
  TheoreticalExact = false
  Type = 5
  UnderTolerance = 0
  X = 38.9277
  Y = 17.9361
FEATURE [TechDraw::DrawProjGroupItem] ProjItem024  label="Top005"
  CoarseView = false
  Direction = (0,0,1)
  Focus = 100
  HardHidden = true
  IsoCount = 0
  IsoHidden = false
  IsoVisible = false
  LockPosition = false
  Perspective = false
  Rotation = 0
  RotationVector = (1,0,0)
  ScaleType = 0
  ScrubCount = 1
  SeamHidden = false
  SeamVisible = false
  SmoothHidden = false
  SmoothVisible = true
  Source = -> [Body009]
  Type = 4
  X = 0
  XDirection = (1,0,0)
  Y = 96.4913
FEATURE [TechDraw::DrawViewDimension] Dimension141
  AngleOverride = false
  Arbitrary = false
  ArbitraryTolerances = false
  BoxCorners = (2) [(-25.6,-37,-1e-07),(25.6,37,1e-07)]
  EqualTolerance = true
  ExtensionAngle = 0
  FormatSpec = %.2w
  FormatSpecOverTolerance = %+.2w
  FormatSpecUnderTolerance = %+.2w
  Inverted = false
  LineAngle = 0
  LockPosition = false
  MeasureType = 1
  OverTolerance = 0
  References2D = -> [ProjItem024]
  Rotation = 0
  ScaleType = 0
  TheoreticalExact = false
  Type = 2
  UnderTolerance = 0
  X = -34.3682
  Y = -41.8605
FEATURE [TechDraw::DrawViewDimension] Dimension142
  AngleOverride = false
  Arbitrary = false
  ArbitraryTolerances = false
  BoxCorners = (2) [(-25.6,-37,-1e-07),(25.6,37,1e-07)]
  EqualTolerance = true
  ExtensionAngle = 0
  FormatSpec = %.2w
  FormatSpecOverTolerance = %+.2w
  FormatSpecUnderTolerance = %+.2w
  Inverted = false
  LineAngle = 0
  LockPosition = false
  MeasureType = 1
  OverTolerance = 0
  References2D = -> [ProjItem024]
  Rotation = 0
  ScaleType = 0
  TheoreticalExact = false
  Type = 6
  UnderTolerance = 0
  X = -9.33028
  Y = -43.9896
FEATURE [TechDraw::DrawViewDimension] Dimension143
  AngleOverride = false
  Arbitrary = false
  ArbitraryTolerances = false
  BoxCorners = (2) [(-25.6,-37,-1e-07),(25.6,37,1e-07)]
  EqualTolerance = true
  ExtensionAngle = 0
  FormatSpec = %.2w x45°
  FormatSpecOverTolerance = %+.2w
  FormatSpecUnderTolerance = %+.2w
  Inverted = false
  LineAngle = 0
  LockPosition = false
  MeasureType = 1
  OverTolerance = 0
  References2D = -> [ProjItem024]
  Rotation = 0
  ScaleType = 0
  TheoreticalExact = false
  Type = 2
  UnderTolerance = 0
  X = 31.6241
  Y = -25.0709
FEATURE [TechDraw::DrawViewDimension] Dimension144
  AngleOverride = false
  Arbitrary = false
  ArbitraryTolerances = false
  BoxCorners = (2) [(-25.6,-37,-1e-07),(25.6,37,1e-07)]
  EqualTolerance = true
  ExtensionAngle = 0
  FormatSpec = %.2w x45°
  FormatSpecOverTolerance = %+.2w
  FormatSpecUnderTolerance = %+.2w
  Inverted = false
  LineAngle = 0
  LockPosition = false
  MeasureType = 1
  OverTolerance = 0
  References2D = -> [ProjItem024]
  Rotation = 0
  ScaleType = 0
  TheoreticalExact = false
  Type = 1
  UnderTolerance = 0
  X = 35.233
  Y = -43.9362
FEATURE [TechDraw::DrawViewDimension] Dimension145
  AngleOverride = false
  Arbitrary = false
  ArbitraryTolerances = false
  BoxCorners = (2) [(-25.6,-37,-1e-07),(25.6,37,1e-07)]
  EqualTolerance = true
  ExtensionAngle = 0
  FormatSpec = ⌀%.2w
  FormatSpecOverTolerance = %+.2w
  FormatSpecUnderTolerance = %+.2w
  Inverted = false
  LineAngle = 0
  LockPosition = false
  MeasureType = 1
  OverTolerance = 0
  References2D = -> [ProjItem024]
  Rotation = 0
  ScaleType = 0
  TheoreticalExact = false
  Type = 5
  UnderTolerance = 0
  X = 33.9663
  Y = 17.6571
FEATURE [TechDraw::DrawViewDimension] Dimension147
  AngleOverride = false
  Arbitrary = false
  ArbitraryTolerances = false
  BoxCorners = (2) [(-25.6,-37,-1e-07),(25.6,37,1e-07)]
  EqualTolerance = true
  ExtensionAngle = 0
  FormatSpec = %.2w
  FormatSpecOverTolerance = %+.2w
  FormatSpecUnderTolerance = %+.2w
  Inverted = false
  LineAngle = 0
  LockPosition = false
  MeasureType = 1
  OverTolerance = 0
  References2D = -> [ProjItem024]
  Rotation = 0
  ScaleType = 0
  TheoreticalExact = false
  Type = 1
  UnderTolerance = 0
  X = 0
  Y = 51.8867
FEATURE [TechDraw::DrawViewDimension] Dimension148
  AngleOverride = false
  Arbitrary = false
  ArbitraryTolerances = false
  BoxCorners = (2) [(-25.6,-37,-1e-07),(25.6,37,1e-07)]
  EqualTolerance = true
  ExtensionAngle = 0
  FormatSpec = %.2w
  FormatSpecOverTolerance = %+.2w
  FormatSpecUnderTolerance = %+.2w
  Inverted = false
  LineAngle = 0
  LockPosition = false
  MeasureType = 1
  OverTolerance = 0
  References2D = -> [ProjItem024]
  Rotation = 0
  ScaleType = 0
  TheoreticalExact = false
  Type = 1
  UnderTolerance = 0
  X = 0
  Y = 58.8867
FEATURE [TechDraw::DrawViewDimension] Dimension151
  AngleOverride = false
  Arbitrary = false
  ArbitraryTolerances = false
  BoxCorners = (2) [(-25.6,-37,-1e-07),(25.6,37,1e-07)]
  EqualTolerance = true
  ExtensionAngle = 0
  FormatSpec = %.2w
  FormatSpecOverTolerance = %+.2w
  FormatSpecUnderTolerance = %+.2w
  Inverted = false
  LineAngle = 0
  LockPosition = false
  MeasureType = 1
  OverTolerance = 0
  References2D = -> [ProjItem024]
  Rotation = 0
  ScaleType = 0
  TheoreticalExact = false
  Type = 2
  UnderTolerance = 0
  X = 43.2087
  Y = 0
FEATURE [TechDraw::DrawViewDimension] Dimension152
  AngleOverride = false
  Arbitrary = false
  ArbitraryTolerances = false
  BoxCorners = (2) [(-25.6,-37,-1e-07),(25.6,37,1e-07)]
  EqualTolerance = true
  ExtensionAngle = 0
  FormatSpec = %.2w
  FormatSpecOverTolerance = %+.2w
  FormatSpecUnderTolerance = %+.2w
  Inverted = false
  LineAngle = 0
  LockPosition = false
  MeasureType = 1
  OverTolerance = 0
  References2D = -> [ProjItem024]
  Rotation = 0
  ScaleType = 0
  TheoreticalExact = false
  Type = 2
  UnderTolerance = 0
  X = -41.3682
  Y = 0
FEATURE [TechDraw::DrawViewDimension] Dimension153
  AngleOverride = false
  Arbitrary = false
  ArbitraryTolerances = false
  BoxCorners = (2) [(-25.6,-37,-1e-07),(25.6,37,1e-07)]
  EqualTolerance = true
  ExtensionAngle = 0
  FormatSpec = %.2w
  FormatSpecOverTolerance = %+.2w
  FormatSpecUnderTolerance = %+.2w
  Inverted = false
  LineAngle = 0
  LockPosition = false
  MeasureType = 1
  OverTolerance = 0
  References2D = -> [ProjItem024]
  Rotation = 0
  ScaleType = 0
  TheoreticalExact = false
  Type = 2
  UnderTolerance = 0
  X = -48.3682
  Y = 0
FEATURE [TechDraw::DrawViewDimension] Dimension154
  AngleOverride = false
  Arbitrary = false
  ArbitraryTolerances = false
  BoxCorners = (2) [(-25.6,-37,-1e-07),(25.6,37,1e-07)]
  EqualTolerance = true
  ExtensionAngle = 0
  FormatSpec = %.2w
  FormatSpecOverTolerance = %+.2w
  FormatSpecUnderTolerance = %+.2w
  Inverted = false
  LineAngle = 0
  LockPosition = false
  MeasureType = 1
  OverTolerance = 0
  References2D = -> [ProjItem024]
  Rotation = 0
  ScaleType = 0
  TheoreticalExact = false
  Type = 2
  UnderTolerance = 0
  X = -34.3682
  Y = -5.76666
FEATURE [TechDraw::DrawViewDimension] Dimension155
  AngleOverride = false
  Arbitrary = false
  ArbitraryTolerances = false
  BoxCorners = (2) [(-25.6,-37,-1e-07),(25.6,37,1e-07)]
  EqualTolerance = true
  ExtensionAngle = 0
  FormatSpec = %.2w
  FormatSpecOverTolerance = %+.2w
  FormatSpecUnderTolerance = %+.2w
  Inverted = false
  LineAngle = 0
  LockPosition = false
  MeasureType = 1
  OverTolerance = 0
  References2D = -> [ProjItem024]
  Rotation = 0
  ScaleType = 0
  TheoreticalExact = false
  Type = 1
  UnderTolerance = 0
  X = 0
  Y = 44.8867
FEATURE [TechDraw::DrawProjGroupItem] ProjItem025  label="FrontTopRight009"
  CoarseView = false
  Direction = (0.57735,-0.57735,0.57735)
  Focus = 100
  HardHidden = false
  IsoCount = 0
  IsoHidden = false
  IsoVisible = false
  LockPosition = false
  Perspective = false
  Rotation = 0
  RotationVector = (1,0,0)
  ScaleType = 0
  ScrubCount = 1
  SeamHidden = false
  SeamVisible = false
  SmoothHidden = false
  SmoothVisible = true
  Source = -> [Body009]
  Type = 7
  X = 137.65
  XDirection = (0.707107,0.707107,0)
  Y = 97.8558
FEATURE [TechDraw::DrawProjGroupItem] ProjItem027  label="FrontTopRight010"
  CoarseView = false
  Direction = (0.57735,-0.57735,0.57735)
  Focus = 100
  HardHidden = false
  IsoCount = 0
  IsoHidden = false
  IsoVisible = false
  LockPosition = false
  Perspective = false
  Rotation = 0
  RotationVector = (1,0,0)
  ScaleType = 0
  ScrubCount = 1
  SeamHidden = false
  SeamVisible = false
  SmoothHidden = false
  SmoothVisible = true
  Source = -> [Body012]
  Type = 7
  X = 98.4918
  XDirection = (0.707107,0.707107,0)
  Y = -15.086
FEATURE [TechDraw::DrawProjGroupItem] ProjItem028  label="Bottom003"
  CoarseView = false
  Direction = (0,0,-1)
  Focus = 100
  HardHidden = true
  IsoCount = 0
  IsoHidden = false
  IsoVisible = false
  LockPosition = false
  Perspective = false
  Rotation = 0
  RotationVector = (1,0,0)
  ScaleType = 0
  ScrubCount = 1
  SeamHidden = false
  SeamVisible = false
  SmoothHidden = false
  SmoothVisible = true
  Source = -> [Body012]
  Type = 5
  X = 0
  XDirection = (1,0,0)
  Y = -99.1434
FEATURE [TechDraw::DrawViewDimension] Dimension167
  AngleOverride = false
  Arbitrary = false
  ArbitraryTolerances = false
  BoxCorners = (2) [(-33.6,-33.6,-1e-07),(33.6,33.6,1e-07)]
  EqualTolerance = true
  ExtensionAngle = 0
  FormatSpec = ⌀%.2w
  FormatSpecOverTolerance = %+.2w
  FormatSpecUnderTolerance = %+.2w
  Inverted = false
  LineAngle = 0
  LockPosition = false
  MeasureType = 1
  OverTolerance = 0
  References2D = -> [ProjItem028]
  Rotation = 0
  ScaleType = 0
  TheoreticalExact = false
  Type = 5
  UnderTolerance = 0
  X = 28.6872
  Y = 14.2557
FEATURE [TechDraw::DrawViewDimension] Dimension168
  AngleOverride = false
  Arbitrary = false
  ArbitraryTolerances = false
  BoxCorners = (2) [(-33.6,-33.6,-1e-07),(33.6,33.6,1e-07)]
  EqualTolerance = true
  ExtensionAngle = 0
  FormatSpec = %.2w
  FormatSpecOverTolerance = %+.2w
  FormatSpecUnderTolerance = %+.2w
  Inverted = false
  LineAngle = 0
  LockPosition = false
  MeasureType = 1
  OverTolerance = 0
  References2D = -> [ProjItem028]
  Rotation = 0
  ScaleType = 0
  TheoreticalExact = false
  Type = 1
  UnderTolerance = 0
  X = 0
  Y = 31.8362
FEATURE [TechDraw::DrawViewDimension] Dimension169
  AngleOverride = false
  Arbitrary = false
  ArbitraryTolerances = false
  BoxCorners = (2) [(-33.6,-33.6,-1e-07),(33.6,33.6,1e-07)]
  EqualTolerance = true
  ExtensionAngle = 0
  FormatSpec = %.2w
  FormatSpecOverTolerance = %+.2w
  FormatSpecUnderTolerance = %+.2w
  Inverted = false
  LineAngle = 0
  LockPosition = false
  MeasureType = 1
  OverTolerance = 0
  References2D = -> [ProjItem028]
  Rotation = 0
  ScaleType = 0
  TheoreticalExact = false
  Type = 2
  UnderTolerance = 0
  X = -32.1581
  Y = 0
FEATURE [TechDraw::DrawViewDimension] Dimension170
  AngleOverride = false
  Arbitrary = false
  ArbitraryTolerances = false
  BoxCorners = (2) [(-33.6,-33.6,-1e-07),(33.6,33.6,1e-07)]
  EqualTolerance = true
  ExtensionAngle = 0
  FormatSpec = %.2w
  FormatSpecOverTolerance = %+.2w
  FormatSpecUnderTolerance = %+.2w
  Inverted = false
  LineAngle = 0
  LockPosition = false
  MeasureType = 1
  OverTolerance = 0
  References2D = -> [ProjItem028]
  Rotation = 0
  ScaleType = 0
  TheoreticalExact = false
  Type = 1
  UnderTolerance = 0
  X = 0
  Y = 24.8362
FEATURE [TechDraw::DrawSVGTemplate] Template006
  Height = 210
  Orientation = 1
  Template = C:/Program Files/FreeCAD 1.0/data/Mod/TechDraw/Templates/A4_Landscape_TD.svg
  Width = 297
FEATURE [TechDraw::DrawSVGTemplate] Template007
  Height = 210
  Orientation = 1
  Template = C:/Program Files/FreeCAD 1.0/data/Mod/TechDraw/Templates/A4_Landscape_TD.svg
  Width = 297
FEATURE [TechDraw::DrawSVGTemplate] Template008
  Height = 210
  Orientation = 1
  Template = C:/Program Files/FreeCAD 1.0/data/Mod/TechDraw/Templates/A4_Landscape_TD.svg
  Width = 297
FEATURE [TechDraw::DrawSVGTemplate] Template009
  EditableTexts = AuthorName=Alex Anastasakis; CheckDate=2024-11-29; CreationDate=2024-11-26; DrawingNumber=11; FC-Scale=1 : 1; FC-Title=Head; SheetNumber=1 / 1; Subtitle=Course: Industrial Design for Game Hardware; SupervisorName=Alvaro Uribe Quevedo; Weight=0.036
  Height = 297
  Orientation = 1
  Template = C:/Program Files/FreeCAD 1.0/data/Mod/TechDraw/Templates/A3_Landscape_TD.svg
  Width = 420
FEATURE [TechDraw::DrawSVGTemplate] Template010
  Height = 210
  Orientation = 1
  Template = C:/Program Files/FreeCAD 1.0/data/Mod/TechDraw/Templates/A4_Landscape_TD.svg
  Width = 297
FEATURE [TechDraw::DrawProjGroupItem] View007  label="Front006"
  CoarseView = false
  Direction = (0,-1,0)
  Focus = 100
  HardHidden = true
  IsoCount = 0
  IsoHidden = false
  IsoVisible = false
  LockPosition = true
  Perspective = false
  Rotation = 0
  RotationVector = (1,0,0)
  Scale = 3
  ScaleType = 2
  ScrubCount = 1
  SeamHidden = false
  SeamVisible = false
  SmoothHidden = false
  SmoothVisible = true
  Source = -> [Body010]
  Type = 0
  X = 0
  XDirection = (1,0,0)
  Y = 0
FEATURE [TechDraw::DrawViewDimension] Dimension113
  AngleOverride = false
  Arbitrary = false
  ArbitraryTolerances = false
  BoxCorners = (2) [(-33.2899,-22.5,-1e-07),(33.2899,22.5,1e-07)]
  EqualTolerance = true
  ExtensionAngle = 0
  FormatSpec = %.2w
  FormatSpecOverTolerance = %+.2w
  FormatSpecUnderTolerance = %+.2w
  Inverted = false
  LineAngle = 0
  LockPosition = false
  MeasureType = 1
  OverTolerance = 0
  References2D = -> [View007]
  Rotation = 0
  Scale = 3
  ScaleType = 0
  TheoreticalExact = false
  Type = 2
  UnderTolerance = 0
  X = -44.9926
  Y = 0
FEATURE [TechDraw::DrawViewDimension] Dimension114
  AngleOverride = false
  Arbitrary = false
  ArbitraryTolerances = false
  BoxCorners = (2) [(-33.2899,-22.5,-1e-07),(33.2899,22.5,1e-07)]
  EqualTolerance = true
  ExtensionAngle = 0
  FormatSpec = %.2w
  FormatSpecOverTolerance = %+.2w
  FormatSpecUnderTolerance = %+.2w
  Inverted = false
  LineAngle = 0
  LockPosition = false
  MeasureType = 1
  OverTolerance = 0
  References2D = -> [View007]
  Rotation = 0
  Scale = 3
  ScaleType = 0
  TheoreticalExact = false
  Type = 0
  UnderTolerance = 0
  X = 44.4365
  Y = 26.4571
FEATURE [TechDraw::DrawViewDimension] Dimension115
  AngleOverride = false
  Arbitrary = false
  ArbitraryTolerances = false
  BoxCorners = (2) [(-33.2899,-22.5,-1e-07),(33.2899,22.5,1e-07)]
  EqualTolerance = true
  ExtensionAngle = 0
  FormatSpec = %.2w
  FormatSpecOverTolerance = %+.2w
  FormatSpecUnderTolerance = %+.2w
  Inverted = false
  LineAngle = 0
  LockPosition = false
  MeasureType = 1
  OverTolerance = 0
  References2D = -> [View007]
  Rotation = 0
  Scale = 3
  ScaleType = 0
  TheoreticalExact = false
  Type = 6
  UnderTolerance = 0
  X = 23.97
  Y = 31.8923
FEATURE [TechDraw::DrawViewDimension] Dimension116
  AngleOverride = false
  Arbitrary = false
  ArbitraryTolerances = false
  BoxCorners = (2) [(-33.2899,-22.5,-1e-07),(33.2899,22.5,1e-07)]
  EqualTolerance = true
  ExtensionAngle = 0
  FormatSpec = %.2w
  FormatSpecOverTolerance = %+.2w
  FormatSpecUnderTolerance = %+.2w
  Inverted = false
  LineAngle = 0
  LockPosition = false
  MeasureType = 1
  OverTolerance = 0
  References2D = -> [View007]
  Rotation = 0
  Scale = 3
  ScaleType = 0
  TheoreticalExact = false
  Type = 6
  UnderTolerance = 0
  X = 32.0771
  Y = -29.7497
FEATURE [TechDraw::DrawProjGroup] ProjGroup006
  Anchor = -> View007
  AutoDistribute = false
  LockPosition = false
  ProjectionType = 1
  Rotation = 0
  Scale = 3
  ScaleType = 0
  Source = -> [Body010]
  Views = -> [View007,ProjItem017,ProjItem018]
  X = 89.975
  Y = 59.878
  spacingX = 15
  spacingY = 15
FEATURE [TechDraw::DrawProjGroupItem] View009  label="Front008"
  CoarseView = false
  Direction = (0,-1,0)
  Focus = 100
  HardHidden = true
  IsoCount = 0
  IsoHidden = false
  IsoVisible = false
  LockPosition = true
  Perspective = false
  Rotation = 0
  RotationVector = (1,0,0)
  Scale = 8
  ScaleType = 2
  ScrubCount = 1
  SeamHidden = false
  SeamVisible = false
  SmoothHidden = false
  SmoothVisible = true
  Source = -> [Body008]
  Type = 0
  X = 0
  XDirection = (1,0,0)
  Y = 0
FEATURE [TechDraw::DrawViewDimension] Dimension131
  AngleOverride = false
  Arbitrary = false
  ArbitraryTolerances = false
  BoxCorners = (2) [(-32,-16,-1e-07),(32,16,1e-07)]
  EqualTolerance = true
  ExtensionAngle = 0
  FormatSpec = %.2w
  FormatSpecOverTolerance = %+.2w
  FormatSpecUnderTolerance = %+.2w
  Inverted = false
  LineAngle = 0
  LockPosition = false
  MeasureType = 1
  OverTolerance = 0
  References2D = -> [View009]
  Rotation = 0
  Scale = 8
  ScaleType = 0
  TheoreticalExact = false
  Type = 0
  UnderTolerance = 0
  X = 40.4062
  Y = 11.2
FEATURE [TechDraw::DrawViewDimension] Dimension132
  AngleOverride = false
  Arbitrary = false
  ArbitraryTolerances = false
  BoxCorners = (2) [(-32,-16,-1e-07),(32,16,1e-07)]
  EqualTolerance = true
  ExtensionAngle = 0
  FormatSpec = %.2w
  FormatSpecOverTolerance = %+.2w
  FormatSpecUnderTolerance = %+.2w
  Inverted = false
  LineAngle = 0
  LockPosition = false
  MeasureType = 1
  OverTolerance = 0
  References2D = -> [View009]
  Rotation = 0
  Scale = 8
  ScaleType = 0
  TheoreticalExact = false
  Type = 2
  UnderTolerance = 0
  X = 47.4062
  Y = 0
FEATURE [TechDraw::DrawProjGroup] ProjGroup008
  Anchor = -> View009
  AutoDistribute = false
  LockPosition = false
  ProjectionType = 1
  Rotation = 0
  Scale = 8
  ScaleType = 0
  Source = -> [Body008]
  Views = -> [View009,ProjItem022,ProjItem023]
  X = 92.2468
  Y = 148.374
  spacingX = 15
  spacingY = 15
FEATURE [TechDraw::DrawPage] Page008  label="Spring_Seat_Drawing"
  KeepUpdated = true
  NextBalloonIndex = 1
  ProjectionType = 1
  Scale = 8
  Template = -> Template008
  Views = -> [ProjGroup008,Dimension131,Dimension132,Dimension135,Dimension136,Dimension137]
FEATURE [TechDraw::DrawProjGroupItem] View010  label="Front009"
  CoarseView = false
  Direction = (0,-1,0)
  Focus = 100
  HardHidden = true
  IsoCount = 0
  IsoHidden = false
  IsoVisible = false
  LockPosition = true
  Perspective = false
  Rotation = 0
  RotationVector = (1,0,0)
  ScaleType = 2
  ScrubCount = 1
  SeamHidden = false
  SeamVisible = false
  SmoothHidden = false
  SmoothVisible = true
  Source = -> [Body009]
  Type = 0
  X = 0
  XDirection = (1,0,0)
  Y = 0
FEATURE [TechDraw::DrawViewDimension] Dimension139
  AngleOverride = false
  Arbitrary = false
  ArbitraryTolerances = false
  BoxCorners = (2) [(-25.6,-20.1,-1e-07),(25.6,20.1,1e-07)]
  EqualTolerance = true
  ExtensionAngle = 0
  FormatSpec = ⌀%.2w
  FormatSpecOverTolerance = %+.2w
  FormatSpecUnderTolerance = %+.2w
  Inverted = false
  LineAngle = 0
  LockPosition = false
  MeasureType = 1
  OverTolerance = 0
  References2D = -> [View010]
  Rotation = 0
  ScaleType = 0
  TheoreticalExact = false
  Type = 5
  UnderTolerance = 0
  X = 43.0231
  Y = 8.01511
FEATURE [TechDraw::DrawViewDimension] Dimension140
  AngleOverride = false
  Arbitrary = false
  ArbitraryTolerances = false
  BoxCorners = (2) [(-25.6,-20.1,-1e-07),(25.6,20.1,1e-07)]
  EqualTolerance = true
  ExtensionAngle = 0
  FormatSpec = ⌀%.2w
  FormatSpecOverTolerance = %+.2w
  FormatSpecUnderTolerance = %+.2w
  Inverted = false
  LineAngle = 0
  LockPosition = false
  MeasureType = 1
  OverTolerance = 0
  References2D = -> [View010]
  Rotation = 0
  ScaleType = 0
  TheoreticalExact = false
  Type = 5
  UnderTolerance = 0
  X = 40.5542
  Y = 18.1542
FEATURE [TechDraw::DrawViewDimension] Dimension165
  AngleOverride = false
  Arbitrary = false
  ArbitraryTolerances = false
  BoxCorners = (2) [(-25.6,-20.1,-1e-07),(25.6,20.1,1e-07)]
  EqualTolerance = true
  ExtensionAngle = 0
  FormatSpec = %.2w
  FormatSpecOverTolerance = %+.2w
  FormatSpecUnderTolerance = %+.2w
  Inverted = false
  LineAngle = 0
  LockPosition = false
  MeasureType = 1
  OverTolerance = 0
  References2D = -> [View010]
  Rotation = 0
  ScaleType = 0
  TheoreticalExact = false
  Type = 0
  UnderTolerance = 0
  X = 35.8478
  Y = -12.8
FEATURE [TechDraw::DrawProjGroup] ProjGroup009
  Anchor = -> View010
  AutoDistribute = false
  LockPosition = false
  ProjectionType = 1
  Rotation = 0
  ScaleType = 0
  Source = -> [Body009]
  Views = -> [View010,ProjItem024,ProjItem025]
  X = 150.248
  Y = 116.92
  spacingX = 15
  spacingY = 15
FEATURE [TechDraw::DrawViewSection] SectionView  label="Section A - A"
  BaseView = -> View010
  Caption = Scale 1 : 1
  CoarseView = false
  CutSurfaceDisplay = 2
  Direction = (-1,0,-1e-16)
  FileGeomPattern = <path>\data\Mod/TechDraw/PAT/FCPAT.pat
  FileHatchPattern = <path>\data\Mod/TechDraw/Patterns/simple.svg
  Focus = 100
  FuseBeforeCut = false
  HardHidden = true
  HatchOffset = (0,0,0)
  HatchRotation = 0
  HatchScale = 1
  IsoCount = 0
  IsoHidden = false
  IsoVisible = false
  LockPosition = false
  NameGeomPattern = Diamond
  Perspective = false
  Rotation = -90
  ScaleType = 0
  ScrubCount = 1
  SeamHidden = false
  SeamVisible = false
  SectionDirection = 4
  SectionLineStretch = 1
  SectionNormal = (-1,0,-1e-16)
  SectionOrigin = (0,0,5.5)
  SmoothHidden = false
  SmoothVisible = true
  TrimAfterCut = false
  UsePreviousCut = false
  X = 276.008
  XDirection = (1e-16,0,-1)
  Y = 116.92
FEATURE [TechDraw::DrawViewDimension] Dimension156
  AngleOverride = false
  Arbitrary = false
  ArbitraryTolerances = false
  BoxCorners = (2) [(-37,-20.1,-1e-07),(37,20.1,1e-07)]
  EqualTolerance = true
  ExtensionAngle = 0
  FormatSpec = %.2w
  FormatSpecOverTolerance = %+.2w
  FormatSpecUnderTolerance = %+.2w
  Inverted = false
  LineAngle = 0
  LockPosition = false
  MeasureType = 1
  OverTolerance = 0
  References2D = -> [SectionView]
  Rotation = 0
  ScaleType = 0
  TheoreticalExact = false
  Type = 2
  UnderTolerance = 0
  X = 44.6371
  Y = 13.6
FEATURE [TechDraw::DrawViewDimension] Dimension161
  AngleOverride = false
  Arbitrary = false
  ArbitraryTolerances = false
  BoxCorners = (2) [(-37,-20.1,-1e-07),(37,20.1,1e-07)]
  EqualTolerance = true
  ExtensionAngle = 0
  FormatSpec = 8x %.2w x45°
  FormatSpecOverTolerance = %+.2w
  FormatSpecUnderTolerance = %+.2w
  Inverted = false
  LineAngle = 0
  LockPosition = false
  MeasureType = 1
  OverTolerance = 0
  References2D = -> [SectionView]
  Rotation = 0
  ScaleType = 0
  TheoreticalExact = false
  Type = 1
  UnderTolerance = 0
  X = 40.723
  Y = -25.5289
FEATURE [TechDraw::DrawViewDimension] Dimension162
  AngleOverride = false
  Arbitrary = false
  ArbitraryTolerances = false
  BoxCorners = (2) [(-37,-20.1,-1e-07),(37,20.1,1e-07)]
  EqualTolerance = true
  ExtensionAngle = 0
  FormatSpec = %.2w
  FormatSpecOverTolerance = %+.2w
  FormatSpecUnderTolerance = %+.2w
  Inverted = false
  LineAngle = 0
  LockPosition = false
  MeasureType = 1
  OverTolerance = 0
  References2D = -> [SectionView]
  Rotation = 0
  ScaleType = 0
  TheoreticalExact = false
  Type = 2
  UnderTolerance = 0
  X = 44.6371
  Y = -8.14659
FEATURE [TechDraw::DrawViewDimension] Dimension163
  AngleOverride = false
  Arbitrary = false
  ArbitraryTolerances = false
  BoxCorners = (2) [(-37,-20.1,-1e-07),(37,20.1,1e-07)]
  EqualTolerance = true
  ExtensionAngle = 0
  FormatSpec = %.2w
  FormatSpecOverTolerance = %+.2w
  FormatSpecUnderTolerance = %+.2w
  Inverted = false
  LineAngle = 0
  LockPosition = false
  MeasureType = 1
  OverTolerance = 0
  References2D = -> [SectionView]
  Rotation = 0
  ScaleType = 0
  TheoreticalExact = false
  Type = 2
  UnderTolerance = 0
  X = -47.1932
  Y = 3.1
FEATURE [TechDraw::DrawViewDimension] Dimension164
  AngleOverride = false
  Arbitrary = false
  ArbitraryTolerances = false
  BoxCorners = (2) [(-37,-20.1,-1e-07),(37,20.1,1e-07)]
  EqualTolerance = true
  ExtensionAngle = 0
  FormatSpec = %.2w
  FormatSpecOverTolerance = %+.2w
  FormatSpecUnderTolerance = %+.2w
  Inverted = false
  LineAngle = 0
  LockPosition = false
  MeasureType = 1
  OverTolerance = 0
  References2D = -> [SectionView]
  Rotation = 0
  ScaleType = 0
  TheoreticalExact = false
  Type = 2
  UnderTolerance = 0
  X = -47.1932
  Y = -16.1
FEATURE [TechDraw::DrawProjGroupItem] View011  label="Front010"
  CoarseView = false
  Direction = (0,-1,0)
  Focus = 100
  HardHidden = true
  IsoCount = 0
  IsoHidden = false
  IsoVisible = false
  LockPosition = true
  Perspective = false
  Rotation = 0
  RotationVector = (1,0,0)
  ScaleType = 2
  ScrubCount = 1
  SeamHidden = false
  SeamVisible = false
  SmoothHidden = false
  SmoothVisible = true
  Source = -> [Body012]
  Type = 0
  X = 0
  XDirection = (1,0,0)
  Y = 0
FEATURE [TechDraw::DrawViewDimension] Dimension171
  AngleOverride = false
  Arbitrary = false
  ArbitraryTolerances = false
  BoxCorners = (2) [(-33.6,-12.6,-1e-07),(33.6,12.6,1e-07)]
  EqualTolerance = true
  ExtensionAngle = 0
  FormatSpec = %.2w
  FormatSpecOverTolerance = %+.2w
  FormatSpecUnderTolerance = %+.2w
  Inverted = false
  LineAngle = 0
  LockPosition = false
  MeasureType = 1
  OverTolerance = 0
  References2D = -> [View011]
  Rotation = 0
  ScaleType = 0
  TheoreticalExact = false
  Type = 2
  UnderTolerance = 0
  X = -11.1793
  Y = 9.60637
FEATURE [TechDraw::DrawViewDimension] Dimension172
  AngleOverride = false
  Arbitrary = false
  ArbitraryTolerances = false
  BoxCorners = (2) [(-16.8,-6.3,-1e-07),(16.8,6.3,1e-07)]
  EqualTolerance = true
  ExtensionAngle = 0
  FormatSpec = ⌀%.2w
  FormatSpecOverTolerance = %+.2w
  FormatSpecUnderTolerance = %+.2w
  Inverted = false
  LineAngle = 0
  LockPosition = false
  MeasureType = 1
  OverTolerance = 0
  References2D = -> [View011]
  Rotation = 0
  ScaleType = 0
  TheoreticalExact = false
  Type = 5
  UnderTolerance = 0
  X = 38.6388
  Y = 3.10078
FEATURE [TechDraw::DrawProjGroup] ProjGroup010
  Anchor = -> View011
  AutoDistribute = false
  LockPosition = false
  ProjectionType = 1
  Rotation = 0
  ScaleType = 0
  Source = -> [Body012]
  Views = -> [View011,ProjItem027,ProjItem028]
  X = 103.23
  Y = 157.573
  spacingX = 15
  spacingY = 15
FEATURE [TechDraw::DrawPage] Page010  label="Head_Top_Drawing"
  KeepUpdated = true
  NextBalloonIndex = 1
  ProjectionType = 1
  Template = -> Template010
  Views = -> [ProjGroup010,Dimension167,Dimension168,Dimension169,Dimension170,Dimension171,Annotation008,Dimension172]
FEATURE [PartDesign::AdditiveHelix] AdditiveHelix002
  Angle = 0
  Axis = (1e-16,1e-16,1)
  Base = (0,0,0)
  BaseFeature = -> AdditiveHelix001
  Growth = 0
  HasBeenEdited = true
  Height = 1.1
  LeftHanded = false
  Mode = 2
  Outside = false
  Pitch = 1.1
  Placement = pos=(0,0,0) rot=(1,0,0;1.5708rad)
  Profile = -> AdditiveHelix001 [Edge1]
  ReferenceAxis = -> Z_Axis021
  Refine = true
  Reversed = true
  Suppressed = false
  Tolerance = 0.1
  Turns = 1
  expr: Height = <<HMRProperties>>.spring_dia + 0.1
FEATURE [PartDesign::Body] Body  label="Spring"
  AllowCompound = false
  Group = -> [Sketch,AdditiveHelix,AdditiveHelix001,AdditiveHelix002]
  Origin = -> Origin021
  Tip = -> AdditiveHelix002
FEATURE [TechDraw::DrawSVGTemplate] Template
  EditableTexts = AuthorName=Alex Anastasakis; CheckDate=2024-11-29; CreationDate=2024-11-27; FC-Scale=1 : 2; FC-Title=Hammer; SheetNumber=1 / 2; Subtitle=Course: Industrial Design for Game Hardware; SupervisorName=Alvaro Uribe Quevedo
  Height = 297
  Orientation = 1
  Template = C:/Program Files/FreeCAD 1.0/data/Mod/TechDraw/Templates/A3_Landscape_TD.svg
  Width = 420
FEATURE [Part::Feature] Body019  label="SpringPusher"
  shape: bbox 23.1 x 23.1 x 14 mm, 29 faces (baked)
FEATURE [Part::Feature] Body020  label="SpringSeat"
  shape: bbox 8 x 8 x 4 mm, 6 faces (baked)
FEATURE [Part::Feature] Body021  label="Head001"
  shape: bbox 51.2 x 74 x 40.79 mm, 56 faces (baked)
FEATURE [Part::Feature] Body022  label="Plug001"
  shape: bbox 22.19 x 22.19 x 15 mm, 8 faces (baked)
FEATURE [Part::Feature] Body023  label="Handle001"
  Placement = pos=(0,0,4.5) rot=(0,0,1;0rad)
  shape: bbox 21.5 x 21.5 x 250 mm, 21 faces (baked)
FEATURE [Part::Feature] Body024  label="HeadTop"
  shape: bbox 33.6 x 33.6 x 12.6 mm, 14 faces (baked)
FEATURE [Part::Feature] Body025  label="Shell001"
  shape: bbox 55.6 x 90 x 55.56 mm, 10 faces (baked)
FEATURE [Part::Feature] Body026  label="FoamL001"
  shape: bbox 50 x 20 x 50 mm, 3 faces (baked)
FEATURE [Part::Feature] Body027  label="FoamS001"
  shape: bbox 8 x 8 x 6 mm, 3 faces (baked)
FEATURE [Part::Feature] Body028  label="Sensor001"
  shape: bbox 30 x 1 x 39.46 mm, 6 faces (baked)
FEATURE [Part::Feature] Body029  label="Spring001"
  shape: bbox 11.19 x 10.92 x 17.1 mm, 9 faces (baked)
FEATURE [App::DocumentObjectGroup] Group004  label="SimpleParts"
  Group = -> [Body019,Body020,Body021,Body022,Body023,Body024,Body025,Body026,Body027,Body028,Body029]
FEATURE [App::Link] SpringPusher  label="SpringPusher001"
  LinkPlacement = pos=(43.8337,3.83366,43.8337) rot=(0,0,1;0rad)
  LinkedObject = -> Body019
  Placement = pos=(43.8337,3.83366,43.8337) rot=(0,0,1;0rad)
FEATURE [App::Link] SpringSeat  label="SpringSeat001"
  LinkPlacement = pos=(23.8337,23.8337,82.1337) rot=(0,0,1;0rad)
  LinkedObject = -> Body020
  Placement = pos=(23.8337,23.8337,82.1337) rot=(0,0,1;0rad)
FEATURE [App::Link] Head001  label="Head002"
  LinkPlacement = pos=(3.83366,103.834,-80.7663) rot=(0,0,1;0rad)
  LinkedObject = -> Body021
  Placement = pos=(3.83366,103.834,-80.7663) rot=(0,0,1;0rad)
FEATURE [App::Link] Plug001  label="Plug002"
  LinkPlacement = pos=(23.8337,23.8337,-264.802) rot=(0,0,1;0rad)
  LinkedObject = -> Body022
  Placement = pos=(23.8337,23.8337,-264.802) rot=(0,0,1;0rad)
FEATURE [App::Link] Handle001  label="Handle002"
  LinkPlacement = pos=(23.8337,23.8337,23.8337) rot=(0,0,1;0rad)
  LinkedObject = -> Body023
  Placement = pos=(23.8337,23.8337,23.8337) rot=(0,0,1;0rad)
FEATURE [App::Link] HeadTop  label="HeadTop001"
  LinkPlacement = pos=(23.8337,23.8337,139.234) rot=(0,0,1;0rad)
  LinkedObject = -> Body024
  Placement = pos=(23.8337,23.8337,139.234) rot=(0,0,1;0rad)
FEATURE [App::Link] Shell001  label="Shell002"
  LinkPlacement = pos=(23.8337,223.834,19.2337) rot=(0,0,1;0rad)
  LinkedObject = -> Body025
  Placement = pos=(23.8337,223.834,19.2337) rot=(0,0,1;0rad)
FEATURE [App::Link] FoamL001  label="FoamL002"
  LinkPlacement = pos=(23.8337,-84.1663,19.2337) rot=(0,0,1;0rad)
  LinkedObject = -> Body026
  Placement = pos=(23.8337,-84.1663,19.2337) rot=(0,0,1;0rad)
FEATURE [App::Link] FoamS001  label="FoamS002"
  LinkPlacement = pos=(23.8337,23.8337,96.2337) rot=(0,0,1;1.5708rad)
  LinkedObject = -> Body027
  Placement = pos=(23.8337,23.8337,96.2337) rot=(0,0,1;1.5708rad)
FEATURE [App::Link] Sensor001  label="Sensor002"
  LinkPlacement = pos=(23.8337,23.8337,117.734) rot=(1,0,0;4.71239rad)
  LinkedObject = -> Body028
  Placement = pos=(23.8337,23.8337,117.734) rot=(1,0,0;4.71239rad)
FEATURE [App::Link] Spring001  label="Spring002"
  LinkPlacement = pos=(23.8337,23.8337,58.1837) rot=(0,0,1;0rad)
  LinkedObject = -> Body029
  Placement = pos=(23.8337,23.8337,58.1837) rot=(0,0,1;0rad)
FEATURE [App::Link] Sensor002  label="Sensor003"
  LinkPlacement = pos=(23.8337,91.3337,19.2337) rot=(0,0,1;0rad)
  LinkedObject = -> Body028
  Placement = pos=(23.8337,91.3337,19.2337) rot=(0,0,1;0rad)
FEATURE [App::Link] Sensor003  label="Sensor004"
  LinkPlacement = pos=(23.8337,-43.6663,19.2337) rot=(0,1,0;1.5708rad)
  LinkedObject = -> Body028
  Placement = pos=(23.8337,-43.6663,19.2337) rot=(0,1,0;1.5708rad)
FEATURE [App::Link] FoamL002  label="FoamL003"
  LinkPlacement = pos=(23.8337,131.834,19.2337) rot=(0,1,0;1.5708rad)
  LinkedObject = -> Body026
  Placement = pos=(23.8337,131.834,19.2337) rot=(0,1,0;1.5708rad)
FEATURE [App::FeaturePython] GroundedJoint  # Assembly grounded joint (typed FeaturePython)
  ObjectToGround = -> Handle001
  Placement = pos=(23.8337,23.8337,23.8337) rot=(0,0,1;0rad)
FEATURE [App::FeaturePython] Joint  label="Fixed"  # Assembly joint (typed FeaturePython)
  Activated = true
  AngleMax = 0
  AngleMin = 0
  Detach1 = false
  Detach2 = false
  Distance = 0
  Distance2 = 0
  EnableAngleMax = false
  EnableAngleMin = false
  EnableLengthMax = false
  EnableLengthMin = false
  JointType = 0 (Fixed)
  LengthMax = 0
  LengthMin = 0
  Placement1 = pos=(0,0,1.6) rot=(0,0,1;0rad)
  Placement2 = pos=(0,3.6e-15,-3) rot=(0,0,1;0rad)
  Reference1 = -> Assembly [Head001.Face8,Head001.Edge1]
  Reference2 = -> Assembly [Handle001.Face1,Handle001.Edge3]
FEATURE [App::FeaturePython] Joint001  label="Fixed001"  # Assembly joint (typed FeaturePython)
  Activated = true
  AngleMax = 0
  AngleMin = 0
  Detach1 = false
  Detach2 = false
  Distance = 0
  Distance2 = 0
  EnableAngleMax = false
  EnableAngleMin = false
  EnableLengthMax = false
  EnableLengthMin = false
  JointType = 0 (Fixed)
  LengthMax = 0
  LengthMin = 0
  Placement2 = pos=(0,3.6e-15,0) rot=(0,0,1;0rad)
  Reference1 = -> Assembly [SpringPusher.Edge5,SpringPusher.Edge5]
  Reference2 = -> Assembly [Handle001.Edge15,Handle001.Edge15]
FEATURE [App::FeaturePython] Joint002  label="Fixed002"  # Assembly joint (typed FeaturePython)
  Activated = true
  AngleMax = 0
  AngleMin = 0
  Detach1 = false
  Detach2 = false
  Distance = 0
  Distance2 = 0
  EnableAngleMax = false
  EnableAngleMin = false
  EnableLengthMax = false
  EnableLengthMin = false
  JointType = 0 (Fixed)
  LengthMax = 0
  LengthMin = 0
  Offset2 = pos=(0,0,1) rot=(0,0,1;0rad)
  Placement1 = pos=(0,0,2.8) rot=(1,0,0;3.14159rad)
  Placement2 = pos=(-4.48237e-07,7.80951e-07,16.75) rot=(0,0,1;0rad)
  Reference1 = -> Assembly [SpringSeat.Edge6,SpringSeat.Edge6]
  Reference2 = -> Assembly [Spring001.Face8,Spring001.Face8]
FEATURE [App::FeaturePython] Joint003  label="Fixed003"  # Assembly joint (typed FeaturePython)
  Activated = true
  AngleMax = 0
  AngleMin = 0
  Detach1 = false
  Detach2 = false
  Distance = 0
  Distance2 = 0
  EnableAngleMax = false
  EnableAngleMin = false
  EnableLengthMax = false
  EnableLengthMin = false
  JointType = 0 (Fixed)
  LengthMax = 0
  LengthMin = 0
  Offset2 = pos=(0,0,1) rot=(0,0,1;0rad)
  Placement1 = pos=(9.05229e-07,1.40084e-11,1.65) rot=(0,0,1;0rad)
  Placement2 = pos=(0,0,-4) rot=(0,0,1;0rad)
  Reference1 = -> Assembly [Spring001.Face2,Spring001.Face2]
  Reference2 = -> Assembly [SpringPusher.Face29,SpringPusher.Face29]
FEATURE [App::FeaturePython] Joint004  label="Fixed004"  # Assembly joint (typed FeaturePython)
  Activated = true
  AngleMax = 0
  AngleMin = 0
  Detach1 = false
  Detach2 = false
  Distance = 0
  Distance2 = 0
  EnableAngleMax = false
  EnableAngleMin = false
  EnableLengthMax = false
  EnableLengthMin = false
  JointType = 0 (Fixed)
  LengthMax = 0
  LengthMin = 0
FEATURE [App::FeaturePython] Joint005  label="Fixed005"  # Assembly joint (typed FeaturePython)
  Activated = true
  AngleMax = 0
  AngleMin = 0
  Detach1 = false
  Detach2 = false
  Distance = 0
  Distance2 = 0
  EnableAngleMax = false
  EnableAngleMin = false
  EnableLengthMax = false
  EnableLengthMin = false
  JointType = 0 (Fixed)
  LengthMax = 0
  LengthMin = 0
  Placement1 = pos=(0,0.5,0) rot=(-1,0,0;4.71239rad)
  Placement2 = pos=(0,0,6) rot=(0,0,1;0rad)
  Reference1 = -> Assembly [Sensor001.Edge3,Sensor001.Edge3]
  Reference2 = -> Assembly [FoamS001.Edge3,FoamS001.Edge3]
FEATURE [App::FeaturePython] Joint006  label="Fixed006"  # Assembly joint (typed FeaturePython)
  Activated = true
  AngleMax = 0
  AngleMin = 0
  Detach1 = false
  Detach2 = false
  Distance = 0
  Distance2 = 0
  EnableAngleMax = false
  EnableAngleMin = false
  EnableLengthMax = false
  EnableLengthMin = false
  JointType = 0 (Fixed)
  LengthMax = 0
  LengthMin = 0
  Offset2 = pos=(0,0,0) rot=(0,0,1;1.5708rad)
  Placement1 = pos=(0,0,19) rot=(1,0,0;3.14159rad)
  Placement2 = pos=(0,-0.5,0) rot=(-1,0,0;1.5708rad)
  Reference1 = -> Assembly [HeadTop.Edge32,HeadTop.Edge32]
  Reference2 = -> Assembly [Sensor001.Face6,Sensor001.Edge1]
FEATURE [App::FeaturePython] Joint007  label="Fixed007"  # Assembly joint (typed FeaturePython)
  Activated = true
  AngleMax = 0
  AngleMin = 0
  Detach1 = false
  Detach2 = false
  Distance = 0
  Distance2 = 0
  EnableAngleMax = false
  EnableAngleMin = false
  EnableLengthMax = false
  EnableLengthMin = false
  JointType = 0 (Fixed)
  LengthMax = 0
  LengthMin = 0
  Placement1 = pos=(0,0.5,0) rot=(-0.57735,-0.57735,-0.57735;2.0944rad)
  Placement2 = pos=(0,0,6) rot=(0,0,1;0rad)
  Reference1 = -> Assembly [Sensor001.Face5,Sensor001.Edge1]
  Reference2 = -> Assembly [FoamS001.Edge3,FoamS001.Edge3]
FEATURE [App::FeaturePython] Joint008  label="Fixed008"  # Assembly joint (typed FeaturePython)
  Activated = true
  AngleMax = 0
  AngleMin = 0
  Detach1 = false
  Detach2 = false
  Distance = 0
  Distance2 = 0
  EnableAngleMax = false
  EnableAngleMin = false
  EnableLengthMax = false
  EnableLengthMin = false
  JointType = 0 (Fixed)
  LengthMax = 0
  LengthMin = 0
  Offset2 = pos=(0,0,-0.2) rot=(0,0,1;0rad)
  Placement1 = pos=(0,16.8,0) rot=(1,0,0;1.5708rad)
  Placement2 = pos=(0,16.8,-2.83e-14) rot=(-1,0,0;1.5708rad)
  Reference1 = -> Assembly [HeadTop.Edge3,HeadTop.Edge3]
  Reference2 = -> Assembly [Head001.Edge22,Head001.Edge22]
FEATURE [App::FeaturePython] Joint009  label="Fixed009"  # Assembly joint (typed FeaturePython)
  Activated = true
  AngleMax = 0
  AngleMin = 0
  Detach1 = false
  Detach2 = false
  Distance = 0
  Distance2 = 0
  EnableAngleMax = false
  EnableAngleMin = false
  EnableLengthMax = false
  EnableLengthMin = false
  JointType = 0 (Fixed)
  LengthMax = 0
  LengthMin = 0
  Placement1 = pos=(0,-0.5,0) rot=(1,0,0;1.5708rad)
  Placement2 = pos=(0,37,0) rot=(1,0,0;1.5708rad)
  Reference1 = -> Assembly [Sensor002.Edge4,Sensor002.Edge4]
  Reference2 = -> Assembly [Head001.Edge112,Head001.Edge112]
FEATURE [App::FeaturePython] Joint010  label="Fixed010"  # Assembly joint (typed FeaturePython)
  Activated = true
  AngleMax = 0
  AngleMin = 0
  Detach1 = false
  Detach2 = false
  Distance = 0
  Distance2 = 0
  EnableAngleMax = false
  EnableAngleMin = false
  EnableLengthMax = false
  EnableLengthMin = false
  JointType = 0 (Fixed)
  LengthMax = 0
  LengthMin = 0
  Placement1 = pos=(-3.6e-15,-10,0) rot=(-0.57735,-0.57735,-0.57735;2.0944rad)
  Placement2 = pos=(0,0.5,0) rot=(1,0,0;1.5708rad)
  Reference1 = -> Assembly [FoamL002.Face3,FoamL002.Edge1]
  Reference2 = -> Assembly [Sensor002.Edge3,Sensor002.Edge3]
FEATURE [App::FeaturePython] Joint011  label="Fixed011"  # Assembly joint (typed FeaturePython)
  Activated = true
  AngleMax = 0
  AngleMin = 0
  Detach1 = false
  Detach2 = false
  Distance = 0
  Distance2 = 0
  EnableAngleMax = false
  EnableAngleMin = false
  EnableLengthMax = false
  EnableLengthMin = false
  JointType = 0 (Fixed)
  LengthMax = 0
  LengthMin = 0
  Placement1 = pos=(0,-0.5,0) rot=(1,0,0;1.5708rad)
  Placement2 = pos=(0,10,0) rot=(1,0,0;1.5708rad)
  Reference1 = -> Assembly [Sensor003.Edge4,Sensor003.Edge4]
  Reference2 = -> Assembly [FoamL001.Edge2,FoamL001.Edge2]
FEATURE [App::FeaturePython] Joint012  label="Fixed012"  # Assembly joint (typed FeaturePython)
  Activated = true
  AngleMax = 0
  AngleMin = 0
  Detach1 = false
  Detach2 = false
  Distance = 0
  Distance2 = 0
  EnableAngleMax = false
  EnableAngleMin = false
  EnableLengthMax = false
  EnableLengthMin = false
  JointType = 0 (Fixed)
  LengthMax = 0
  LengthMin = 0
  Placement1 = pos=(0,0,0) rot=(1,0,0;1.5708rad)
  Placement2 = pos=(0,-1.84017e-07,0) rot=(1,0,0;1.5708rad)
  Reference1 = -> Assembly [Head001.Face2,Head001.Face2]
  Reference2 = -> Assembly [Shell001.Face10,Shell001.Face10]
FEATURE [App::FeaturePython] Joint013  label="Fixed013"  # Assembly joint (typed FeaturePython)
  Activated = true
  AngleMax = 0
  AngleMin = 0
  Detach1 = false
  Detach2 = false
  Distance = 0
  Distance2 = 0
  EnableAngleMax = false
  EnableAngleMin = false
  EnableLengthMax = false
  EnableLengthMin = false
  JointType = 0 (Fixed)
  LengthMax = 0
  LengthMin = 0
  Offset2 = pos=(0,0,5) rot=(0,0,1;0rad)
  Placement1 = pos=(0,3.6e-15,13.636) rot=(1,0,0;3.14159rad)
  Placement2 = pos=(0,-4.86e-14,-245) rot=(0,0,1;0rad)
  Reference1 = -> Assembly [Plug001.Edge9,Plug001.Edge9]
  Reference2 = -> Assembly [Handle001.Edge25,Handle001.Edge25]
FEATURE [App::FeaturePython] Joint014  label="Fixed014"  # Assembly joint (typed FeaturePython)
  Activated = true
  AngleMax = 0
  AngleMin = 0
  Detach1 = false
  Detach2 = false
  Distance = 0
  Distance2 = 0
  EnableAngleMax = false
  EnableAngleMin = false
  EnableLengthMax = false
  EnableLengthMin = false
  JointType = 0 (Fixed)
  LengthMax = 0
  LengthMin = 0
  Placement1 = pos=(0,0.5,0) rot=(-0.57735,-0.57735,-0.57735;2.0944rad)
  Placement2 = pos=(0,-37,1.42e-14) rot=(1,0,0;1.5708rad)
  Reference1 = -> Assembly [Sensor003.Face5,Sensor003.Edge1]
  Reference2 = -> Assembly [Head001.Edge114,Head001.Edge114]
FEATURE [Assembly::JointGroup] Joints
  Group = -> [GroundedJoint,Joint,Joint001,Joint002,Joint003,Joint004,Joint005,Joint006,Joint007,Joint008,Joint009,Joint010,Joint011,Joint012,Joint013,Joint014]
FEATURE [Assembly::AssemblyObject] Assembly  label="HammerAssembly"
  Group = -> [Joints,SpringPusher,SpringSeat,Head001,Plug001,Handle001,HeadTop,Shell001,FoamL001,FoamS001,Sensor001,Spring001,Sensor002,Sensor003,FoamL002,GroundedJoint,Joint,Joint001,Joint002,Joint003,Joint004,Joint005,Joint006,Joint007,Joint008,Joint009,Joint010,Joint011,Joint012,Joint013,Joint014]
  Origin = -> Origin
  Type = Assembly
FEATURE [App::DocumentObjectGroupPython] SimpleGroup013  # scripted group (container) (typed FeaturePython)
  AnimationStepTime = 0
  AnimationSteps = 5
  Distance = 20
  Revolutions = 0
  dir_vectors = (1) [(-1,0,0)]
  rot_centers = (1) [(12.2837,23.8337,25.9935)]
  rot_vectors = (1) [(-1,0,0)]
FEATURE [App::DocumentObjectGroupPython] SimpleGroup014  # scripted group (container) (typed FeaturePython)
  AnimationStepTime = 0
  AnimationSteps = 20
  Distance = 80
  Revolutions = 0
  dir_vectors = (1) [(0,1,-2.2e-16)]
  rot_centers = (1) [(-26.1663,58.8337,-276.033)]
  rot_vectors = (1) [(0,1,-2.2e-16)]
FEATURE [App::DocumentObjectGroupPython] SimpleGroup015  # scripted group (container) (typed FeaturePython)
  AnimationStepTime = 0
  AnimationSteps = 20
  Distance = 200
  Revolutions = 0
  dir_vectors = (1) [(0,2.2e-16,1)]
  rot_centers = (1) [(-26.1663,123.834,-268.166)]
  rot_vectors = (1) [(0,2.2e-16,1)]
FEATURE [App::DocumentObjectGroupPython] SimpleGroup016  # scripted group (container) (typed FeaturePython)
  AnimationStepTime = 0
  AnimationSteps = 10
  Distance = 20
  Revolutions = 0
  dir_vectors = (1) [(0,0,1)]
  rot_centers = (1) [(23.8337,23.8337,28.8337)]
  rot_vectors = (1) [(0,0,1)]
FEATURE [App::DocumentObjectGroupPython] SimpleGroup017  # scripted group (container) (typed FeaturePython)
  AnimationStepTime = 0
  AnimationSteps = 10
  Distance = 20
  Revolutions = 0
  dir_vectors = (1) [(1,0,0)]
  rot_centers = (1) [(35.3837,23.8337,45.9935)]
  rot_vectors = (1) [(1,0,0)]
FEATURE [App::DocumentObjectGroupPython] SimpleGroup018  # scripted group (container) (typed FeaturePython)
  AnimationStepTime = 0
  AnimationSteps = 10
  Distance = 20
  Revolutions = 0
  dir_vectors = (1) [(0,-1,0)]
  rot_centers = (1) [(43.8337,12.2837,45.9935)]
  rot_vectors = (1) [(0,-1,0)]
FEATURE [Part::Feature] trajectory_line
  shape: bbox 2e-07 x 200 x 2e-07 mm, 0 faces, 0 solids (baked)
FEATURE [App::DocumentObjectGroupPython] SimpleGroup  # scripted group (container) (typed FeaturePython)
  AnimationStepTime = 0
  AnimationSteps = 20
  Distance = -200
  Group = -> [trajectory_line]
  Revolutions = 0
  dir_vectors = (1) [(0,-1,0)]
  rot_centers = (1) [(23.8337,-21.1663,19.7198)]
  rot_vectors = (1) [(0,-1,0)]
FEATURE [Part::Feature] trajectory_line001
  shape: bbox 2e-07 x 2e-07 x 80 mm, 0 faces, 0 solids (baked)
FEATURE [App::DocumentObjectGroupPython] SimpleGroup002  # scripted group (container) (typed FeaturePython)
  AnimationStepTime = 0
  AnimationSteps = 20
  Distance = 80
  Group = -> [trajectory_line001]
  Revolutions = 0
  dir_vectors = (3) [(0,0,1),(0,0,1),(0,0,1)]
  rot_centers = (3) [(23.8337,23.8337,28.8337),(23.8337,23.8337,28.8337),(23.8337,23.8337,28.8337)]
  rot_vectors = (3) [(0,0,1),(0,0,1),(0,0,1)]
FEATURE [Part::Feature] trajectory_line002
  shape: bbox 2e-07 x 2e-07 x 40 mm, 0 faces, 0 solids (baked)
FEATURE [App::DocumentObjectGroupPython] SimpleGroup003  # scripted group (container) (typed FeaturePython)
  AnimationStepTime = 0
  AnimationSteps = 20
  Distance = 40
  Group = -> [trajectory_line002]
  Revolutions = 0
  dir_vectors = (2) [(0,0,1),(0,0,1)]
  rot_centers = (2) [(23.8337,23.8337,28.8337),(23.8337,23.8337,28.8337)]
  rot_vectors = (2) [(0,0,1),(0,0,1)]
FEATURE [Part::Feature] trajectory_line003
  shape: bbox 2e-07 x 2e-07 x 10 mm, 0 faces, 0 solids (baked)
FEATURE [App::DocumentObjectGroupPython] SimpleGroup004  # scripted group (container) (typed FeaturePython)
  AnimationStepTime = 0
  AnimationSteps = 10
  Distance = 10
  Group = -> [trajectory_line003]
  Revolutions = 0
  dir_vectors = (1) [(0,2.2e-16,1)]
  rot_centers = (1) [(23.8337,23.8337,76.1337)]
  rot_vectors = (1) [(0,2.2e-16,1)]
FEATURE [Part::Feature] trajectory_line004
  shape: bbox 2e-07 x 2e-07 x 40 mm, 0 faces, 0 solids (baked)
FEATURE [App::DocumentObjectGroupPython] SimpleGroup005  # scripted group (container) (typed FeaturePython)
  AnimationStepTime = 0
  AnimationSteps = 20
  Distance = 40
  Group = -> [trajectory_line004]
  Revolutions = 0
  dir_vectors = (1) [(0,2.2e-16,1)]
  rot_centers = (1) [(23.8337,23.8337,86.1337)]
  rot_vectors = (1) [(0,2.2e-16,1)]
FEATURE [Part::Feature] trajectory_line005
  shape: bbox 2e-07 x 2e-07 x 15 mm, 0 faces, 0 solids (baked)
FEATURE [App::DocumentObjectGroupPython] SimpleGroup006  # scripted group (container) (typed FeaturePython)
  AnimationStepTime = 0
  AnimationSteps = 20
  Distance = 15
  Group = -> [trajectory_line005]
  Revolutions = 0
  dir_vectors = (1) [(2.46973e-31,-4.46134e-16,-1)]
  rot_centers = (1) [(23.8337,23.8337,111.234)]
  rot_vectors = (1) [(2.46973e-31,-4.46134e-16,-1)]
FEATURE [Part::Feature] trajectory_line006
  shape: bbox 2e-07 x 2e-07 x 30 mm, 0 faces, 0 solids (baked)
FEATURE [App::DocumentObjectGroupPython] SimpleGroup007  # scripted group (container) (typed FeaturePython)
  AnimationStepTime = 0
  AnimationSteps = 20
  Distance = 30
  Group = -> [trajectory_line006]
  Revolutions = 0
  dir_vectors = (1) [(0,-2.2e-16,-1)]
  rot_centers = (1) [(23.8337,23.8337,-234.802)]
  rot_vectors = (1) [(0,-2.2e-16,-1)]
FEATURE [Part::Feature] trajectory_line007
  shape: bbox 2e-07 x 60 x 2e-07 mm, 0 faces, 0 solids (baked)
FEATURE [App::DocumentObjectGroupPython] SimpleGroup008  # scripted group (container) (typed FeaturePython)
  AnimationStepTime = 0
  AnimationSteps = 10
  Distance = 60
  Group = -> [trajectory_line007]
  Revolutions = 0
  dir_vectors = (2) [(0,-1,2.2e-16),(0,-1,2.2e-16)]
  rot_centers = (2) [(23.8337,-11.1663,23.9665),(23.8337,-11.1663,23.9665)]
  rot_vectors = (2) [(0,-1,2.2e-16),(0,-1,2.2e-16)]
FEATURE [Part::Feature] trajectory_line008
  shape: bbox 2e-07 x 30 x 2e-07 mm, 0 faces, 0 solids (baked)
FEATURE [App::DocumentObjectGroupPython] SimpleGroup009  # scripted group (container) (typed FeaturePython)
  AnimationStepTime = 0
  AnimationSteps = 10
  Distance = 30
  Group = -> [trajectory_line008]
  Revolutions = 0
  dir_vectors = (1) [(2.2e-16,1,4.88498e-32)]
  rot_centers = (1) [(21.9026,-73.1663,19.2337)]
  rot_vectors = (1) [(2.2e-16,1,4.88498e-32)]
FEATURE [Part::Feature] trajectory_line009
  shape: bbox 2e-07 x 60 x 2e-07 mm, 0 faces, 0 solids (baked)
FEATURE [App::DocumentObjectGroupPython] SimpleGroup010  # scripted group (container) (typed FeaturePython)
  AnimationStepTime = 0
  AnimationSteps = 10
  Distance = 60
  Group = -> [trajectory_line009]
  Revolutions = 0
  dir_vectors = (2) [(0,1,-2.2e-16),(0,1,-2.2e-16)]
  rot_centers = (2) [(23.8337,58.8337,23.9665),(23.8337,58.8337,23.9665)]
  rot_vectors = (2) [(0,1,-2.2e-16),(0,1,-2.2e-16)]
FEATURE [Part::Feature] trajectory_line010
  shape: bbox 2e-07 x 30 x 2e-07 mm, 0 faces, 0 solids (baked)
FEATURE [App::DocumentObjectGroupPython] SimpleGroup011  # scripted group (container) (typed FeaturePython)
  AnimationStepTime = 0
  AnimationSteps = 10
  Distance = 30
  Group = -> [trajectory_line010]
  Revolutions = 0
  dir_vectors = (1) [(0,-1,-2.2e-16)]
  rot_centers = (1) [(23.8337,120.834,17.3026)]
  rot_vectors = (1) [(0,-1,-2.2e-16)]
FEATURE [Part::Feature] trajectory_line011
  shape: bbox 2e-07 x 2e-07 x 300 mm, 0 faces, 0 solids (baked)
FEATURE [App::DocumentObjectGroupPython] SimpleGroup012  # scripted group (container) (typed FeaturePython)
  AnimationStepTime = 0
  AnimationSteps = 20
  Distance = 300
  Group = -> [trajectory_line011]
  Revolutions = 0
  dir_vectors = (1) [(0,-6.7e-16,-1)]
  rot_centers = (1) [(23.8337,23.8337,4.63366)]
  rot_vectors = (1) [(0,-6.7e-16,-1)]
FEATURE [App::DocumentObjectGroupPython] ExplodedAssembly  # scripted group (container) (typed FeaturePython)
  AnimationStep = 0
  CurrentTrajectory = -1
  Group = -> [SimpleGroup,SimpleGroup002,SimpleGroup003,SimpleGroup004,SimpleGroup005,SimpleGroup006,SimpleGroup007,SimpleGroup008,SimpleGroup009,SimpleGroup010,SimpleGroup011,SimpleGroup012,SimpleGroup013,SimpleGroup014,SimpleGroup015,SimpleGroup016,SimpleGroup017,SimpleGroup018]
  InAnimation = false
  RemoveAllTrajectories = false
  ResetAnimation = false
FEATURE [TechDraw::DrawProjGroupItem] View
  CoarseView = false
  Direction = (-0.57735,-0.57735,0.57735)
  Focus = 100
  HardHidden = false
  IsoCount = 0
  IsoHidden = false
  IsoVisible = false
  LockPosition = false
  Perspective = false
  Rotation = 0
  RotationVector = (1,0,0)
  Scale = 0.5
  ScaleType = 0
  ScrubCount = 1
  SeamHidden = false
  SeamVisible = false
  SmoothHidden = false
  SmoothVisible = true
  Source = -> [Assembly]
  Type = 0
  X = 89.3936
  XDirection = (0.707107,-0.707107,0)
  Y = 134.943
FEATURE [Spreadsheet::Sheet] Spreadsheet  label="BOM"
  cells = A1='PARTS LIST; A2='ITEM NO.; B2='QTY; C2='NAME; D2='PART DESCRIPTION; E2='MATERIAL; F2='COST; A3=1; B3=1; C3='Shell; D3='Hammer head reinforcement; E3='PVC; F3='$19.49 (tube of PVC); A4=2; B4=2; C4='Large Foam Disc; D4='50mm diameter, 20mm thick; E4='Polyethylene Foam; F4='$26.99 (pack of foam); A5=3; B5=3; C5='Sensor; D5='Force sensor; E5='Plastic/Metal; F5='$14.19ea; A6=4; B6=1; C6='Head Top Cover; D6='Cover for top sensor; E6='PLA; F6='$22.99 (1kg of filament); A7=5; B7=1; C7='Small Foam Disc; D7='8mm diameter, 6mm thick; E7='Foam; F7='Shares cost of item NO. 2; A8=6; B8=1; C8='Spring Seat; D8='Flat top for the spring; E8='PLA; F8='Shares cost of item NO. 4; A9=7; B9=1; C9='Spring; D9='8mm OD x 15mm long; E9='Steel; F9='$10.39 (pack of 5); A10=8; B10=1; C10='Pusher; D10='Holds the spring; E10='PLA; F10='Shares cost of item NO. 4; A11=9; B11=1; C11='Handle; E11='Metal; F11='$19.99 (broom stick with desired handle); A12=10; B12=1; C12='Plug; D12='Makes a smaller hole for cable management; E12='PLA; F12='Shares cost of item NO. 4; A13=11; B13=1; C13='Head; D13='Holds everything together; E13='PLA; F13='Shares cost of item NO. 4; A14='Note: costs are based off of amazon.ca prices.
FEATURE [TechDraw::DrawViewSpreadsheet] Sheet
  CellEnd = f13
  CellStart = A1
  Font = osifont
  LineWidth = 0.35
  LockPosition = false
  Rotation = 0
  ScaleType = 2
  Source = -> Spreadsheet
  Symbol = <blob: 15819 chars omitted>
  TextSize = 12
  X = 303.093
  Y = 234.742
FEATURE [TechDraw::DrawViewBalloon] Balloon
  BubbleShape = 0
  EndType = 0
  EndTypeScale = 1
  KinkLength = 5
  LockPosition = false
  OriginX = -84.2403
  OriginY = 161.914
  Rotation = 0
  Scale = 0.5
  ScaleType = 0
  ShapeScale = 1
  SourceView = -> View
  Text = 1
  TextWrapLen = -1
  X = -115.241
  Y = 210.245
FEATURE [TechDraw::DrawViewBalloon] Balloon001
  BubbleShape = 0
  EndType = 0
  EndTypeScale = 1
  KinkLength = 5
  LockPosition = false
  OriginX = -25.1938
  OriginY = 124.602
  Rotation = 0
  Scale = 0.5
  ScaleType = 0
  ShapeScale = 1
  SourceView = -> Balloon
  Text = 2
  TextWrapLen = -1
  X = -62.3527
  Y = 210.608
FEATURE [TechDraw::DrawViewBalloon] Balloon002
  BubbleShape = 0
  EndType = 0
  EndTypeScale = 1
  KinkLength = 5
  LockPosition = false
  OriginX = 4.51059
  OriginY = 96.7088
  Rotation = 0
  Scale = 0.5
  ScaleType = 0
  ShapeScale = 1
  SourceView = -> Balloon001
  Text = 3
  TextWrapLen = -1
  X = -15.6227
  Y = 210.608
FEATURE [TechDraw::DrawViewBalloon] Balloon003
  BubbleShape = 0
  EndType = 0
  EndTypeScale = 1
  KinkLength = 5
  LockPosition = false
  OriginX = 32.0765
  OriginY = 179.166
  Rotation = 0
  Scale = 0.5
  ScaleType = 0
  ShapeScale = 1
  SourceView = -> View
  Text = 4
  TextWrapLen = -1
  X = 59.0356
  Y = 210.11
FEATURE [TechDraw::DrawViewBalloon] Balloon004
  BubbleShape = 0
  EndType = 0
  EndTypeScale = 1
  KinkLength = 5
  LockPosition = false
  OriginX = 50.5162
  OriginY = 119.53
  Rotation = 0
  Scale = 0.5
  ScaleType = 0
  ShapeScale = 1
  SourceView = -> View
  Text = 5
  TextWrapLen = -1
  X = 122.756
  Y = 209.159
FEATURE [TechDraw::DrawViewBalloon] Balloon005
  BubbleShape = 0
  EndType = 0
  EndTypeScale = 1
  KinkLength = 5
  LockPosition = false
  OriginX = 50.5162
  OriginY = 109.025
  Rotation = 0
  Scale = 0.5
  ScaleType = 0
  ShapeScale = 1
  SourceView = -> View
  Text = 6
  TextWrapLen = -1
  X = 166.77
  Y = 165.93
FEATURE [TechDraw::DrawViewBalloon] Balloon006
  BubbleShape = 0
  EndType = 0
  EndTypeScale = 1
  KinkLength = 5
  LockPosition = false
  OriginX = 50.1539
  OriginY = 98.1578
  Rotation = 0
  Scale = 0.5
  ScaleType = 0
  ShapeScale = 1
  SourceView = -> Balloon005
  Text = 7
  TextWrapLen = -1
  X = 165.502
  Y = 129.102
FEATURE [TechDraw::DrawViewBalloon] Balloon007
  BubbleShape = 0
  EndType = 0
  EndTypeScale = 1
  KinkLength = 5
  LockPosition = false
  OriginX = 88.19
  OriginY = 81.4944
  Rotation = 0
  Scale = 0.5
  ScaleType = 0
  ShapeScale = 1
  SourceView = -> Balloon006
  Text = 8
  TextWrapLen = -1
  X = 166.981
  Y = 95.0502
FEATURE [TechDraw::DrawViewBalloon] Balloon008
  BubbleShape = 0
  EndType = 0
  EndTypeScale = 1
  KinkLength = 5
  LockPosition = false
  OriginX = 57.0366
  OriginY = -54.7111
  Rotation = 0
  Scale = 0.5
  ScaleType = 0
  ShapeScale = 1
  SourceView = -> Balloon007
  Text = 9
  TextWrapLen = -1
  X = 166.619
  Y = -29.4123
FEATURE [TechDraw::DrawViewBalloon] Balloon009
  BubbleShape = 0
  EndType = 0
  EndTypeScale = 1
  KinkLength = 5
  LockPosition = false
  OriginX = 57.0366
  OriginY = -168.819
  Rotation = 0
  Scale = 0.5
  ScaleType = 0
  ShapeScale = 1
  SourceView = -> Balloon008
  Text = 10
  TextWrapLen = -1
  X = 165.502
  Y = -141.86
FEATURE [TechDraw::DrawViewBalloon] Balloon010
  BubbleShape = 0
  EndType = 0
  EndTypeScale = 1
  KinkLength = 5
  LockPosition = false
  OriginX = -38.597
  OriginY = -24.2822
  Rotation = 0
  Scale = 0.5
  ScaleType = 0
  ShapeScale = 1
  SourceView = -> Balloon009
  Text = 11
  TextWrapLen = -1
  X = -90.9704
  Y = -213.586
FEATURE [TechDraw::DrawPage] Page  label="ExplodedView"
  KeepUpdated = false
  NextBalloonIndex = 12
  ProjectionType = 1
  Scale = 0.5
  Template = -> Template
  Views = -> [View,Sheet,Balloon,Balloon003,Balloon004,Balloon005,Balloon001,Balloon002,Balloon006,Balloon007,Balloon008,Balloon009,Balloon010]
FEATURE [TechDraw::DrawSVGTemplate] Template011
  EditableTexts = AuthorName=Alex Anastasakis; CheckDate=2024-11-29; CreationDate=2024-11-27; FC-Scale=1 : 2; FC-Title=Hammer; SheetNumber=2 / 2; Subtitle=Course: Industrial Design for Game Hardware; SupervisorName=Alvaro Uribe Quevedo
  Height = 297
  Orientation = 1
  Template = C:/Program Files/FreeCAD 1.0/data/Mod/TechDraw/Templates/A3_Landscape_TD.svg
  Width = 420
FEATURE [App::DocumentObjectGroup] Group005  label="ExplodedViewBalloonsAndBOM"
  Group = -> [Balloon001,Balloon002,Balloon006,Balloon007,Balloon008,Balloon009,Balloon010,Spreadsheet]
FEATURE [TechDraw::DrawProjGroupItem] View012  label="Front"
  CoarseView = false
  Direction = (0,-1,0)
  Focus = 100
  HardHidden = false
  IsoCount = 0
  IsoHidden = false
  IsoVisible = false
  LockPosition = true
  Perspective = false
  Rotation = 0
  RotationVector = (1,0,0)
  Scale = 0.5
  ScaleType = 2
  ScrubCount = 1
  SeamHidden = false
  SeamVisible = false
  SmoothHidden = false
  SmoothVisible = true
  Source = -> [Assembly]
  Type = 0
  X = 0
  XDirection = (1,0,0)
  Y = 0
FEATURE [TechDraw::DrawProjGroupItem] ProjItem029  label="FrontTopRight"
  CoarseView = false
  Direction = (0.57735,-0.57735,0.57735)
  Focus = 100
  HardHidden = false
  IsoCount = 0
  IsoHidden = false
  IsoVisible = false
  LockPosition = false
  Perspective = false
  Rotation = 0
  RotationVector = (1,0,0)
  Scale = 0.5
  ScaleType = 0
  ScrubCount = 1
  SeamHidden = false
  SeamVisible = false
  SmoothHidden = false
  SmoothVisible = true
  Source = -> [Assembly]
  Type = 7
  X = 103.833
  XDirection = (0.707107,0.707107,0)
  Y = 12.3789
FEATURE [TechDraw::DrawProjGroupItem] ProjItem  label="Left"
  CoarseView = false
  Direction = (-1,-1e-16,0)
  Focus = 100
  HardHidden = false
  IsoCount = 0
  IsoHidden = false
  IsoVisible = false
  LockPosition = false
  Perspective = false
  Rotation = 0
  RotationVector = (1,0,0)
  ScaleType = 2
  ScrubCount = 1
  SeamHidden = false
  SeamVisible = false
  SmoothHidden = false
  SmoothVisible = true
  Source = -> [Assembly]
  Type = 1
  X = -95.6711
  XDirection = (1e-16,-1,0)
  Y = 0
FEATURE [TechDraw::DrawProjGroupItem] ProjItem030  label="Bottom"
  CoarseView = false
  Direction = (0,0,-1)
  Focus = 100
  HardHidden = false
  IsoCount = 0
  IsoHidden = false
  IsoVisible = false
  LockPosition = false
  Perspective = false
  Rotation = 0
  RotationVector = (1,0,0)
  ScaleType = 2
  ScrubCount = 1
  SeamHidden = false
  SeamVisible = false
  SmoothHidden = false
  SmoothVisible = true
  Source = -> [Assembly]
  Type = 5
  X = 0
  XDirection = (1,0,0)
  Y = -121.07
FEATURE [TechDraw::DrawProjGroup] ProjGroup
  Anchor = -> View012
  AutoDistribute = false
  LockPosition = false
  ProjectionType = 1
  Rotation = 0
  Scale = 0.5
  ScaleType = 0
  Source = -> [Assembly]
  Views = -> [View012,ProjItem029,ProjItem,ProjItem030]
  X = 184.396
  Y = 180.108
  spacingX = 15
  spacingY = 15
FEATURE [TechDraw::DrawPage] Page011  label="AssemblyDrawing"
  KeepUpdated = true
  NextBalloonIndex = 1
  ProjectionType = 1
  Scale = 0.5
  Template = -> Template011
  Views = -> [ProjGroup]
FEATURE [TechDraw::DrawViewAnnotation] Annotation
  Font = osifont
  LineSpace = 100
  LockPosition = false
  MaxWidth = -1
  Rotation = 0
  Scale = 3
  ScaleType = 0
  Text = Changes: | Added chamfers and small adjustments to dimentions.
  TextSize = 4
  TextStyle = 0
  X = 216.023
  Y = 77.5046
FEATURE [TechDraw::DrawPage] Page006  label="Plug_Drawing"
  KeepUpdated = true
  NextBalloonIndex = 1
  ProjectionType = 1
  Scale = 3
  Template = -> Template006
  Views = -> [ProjGroup006,Dimension113,Dimension114,Dimension115,Dimension116,Dimension117,Dimension118,Dimension119,Annotation]
FEATURE [TechDraw::DrawViewDimension] Dimension
  AngleOverride = false
  Arbitrary = false
  ArbitraryTolerances = false
  BoxCorners = (2) [(-37,-20.1,-1e-07),(37,20.1,1e-07)]
  EqualTolerance = true
  ExtensionAngle = 0
  FormatSpec = %.2w
  FormatSpecOverTolerance = %+.2w
  FormatSpecUnderTolerance = %+.2w
  Inverted = false
  LineAngle = 0
  LockPosition = false
  MeasureType = 1
  OverTolerance = 0
  References2D = -> [SectionView]
  Rotation = 0
  ScaleType = 0
  TheoreticalExact = false
  Type = 0
  UnderTolerance = 0
  X = 8.81345
  Y = 29.1203
FEATURE [TechDraw::DrawPage] Page009  label="Head_Drawing"
  KeepUpdated = true
  NextBalloonIndex = 1
  ProjectionType = 1
  Template = -> Template009
  Views = -> [ProjGroup009,SectionView,Annotation004,Annotation005,Dimension139,Dimension140,Dimension141,Dimension142,Dimension143,Dimension144,Dimension145,Dimension147,Dimension148,Dimension151,Dimension152,Dimension153,Dimension154,Dimension155,Dimension156,Dimension161,Dimension162,Dimension163,Dimension164,Dimension165,Annotation006,Dimension]
FEATURE [TechDraw::DrawSVGTemplate] Template012
  Height = 210
  Orientation = 1
  Template = C:/Program Files/FreeCAD 1.0/data/Mod/TechDraw/Templates/A4_Landscape_TD.svg
  Width = 297
FEATURE [TechDraw::DrawProjGroupItem] View013  label="Front011"
  CoarseView = false
  Direction = (0,-1,0)
  Focus = 100
  HardHidden = true
  IsoCount = 0
  IsoHidden = false
  IsoVisible = false
  LockPosition = true
  Perspective = false
  Rotation = 0
  RotationVector = (1,0,0)
  Scale = 0.5
  ScaleType = 2
  ScrubCount = 1
  SeamHidden = false
  SeamVisible = false
  SmoothHidden = false
  SmoothVisible = true
  Source = -> [Body011]
  Type = 0
  X = 0
  XDirection = (1,0,0)
  Y = 0
FEATURE [TechDraw::DrawProjGroupItem] ProjItem031  label="Top"
  CoarseView = false
  Direction = (0,0,1)
  Focus = 100
  HardHidden = true
  IsoCount = 0
  IsoHidden = false
  IsoVisible = false
  LockPosition = false
  Perspective = false
  Rotation = 0
  RotationVector = (1,0,0)
  Scale = 0.5
  ScaleType = 0
  ScrubCount = 1
  SeamHidden = false
  SeamVisible = false
  SmoothHidden = false
  SmoothVisible = true
  Source = -> [Body011]
  Type = 4
  X = 0
  XDirection = (1,0,0)
  Y = 94.9907
FEATURE [TechDraw::DrawProjGroupItem] ProjItem032  label="FrontTopRight011"
  CoarseView = false
  Direction = (0.57735,-0.57735,0.57735)
  Focus = 100
  HardHidden = false
  IsoCount = 0
  IsoHidden = false
  IsoVisible = false
  LockPosition = false
  Perspective = false
  Rotation = 0
  RotationVector = (1,0,0)
  Scale = 0.5
  ScaleType = 0
  ScrubCount = 1
  SeamHidden = false
  SeamVisible = false
  SmoothHidden = false
  SmoothVisible = true
  Source = -> [Body011]
  Type = 7
  X = 68.7229
  XDirection = (0.707107,0.707107,0)
  Y = 55.8334
FEATURE [TechDraw::DrawProjGroup] ProjGroup011
  Anchor = -> View013
  AutoDistribute = false
  LockPosition = false
  ProjectionType = 1
  Rotation = 0
  Scale = 0.5
  ScaleType = 0
  Source = -> [Body011]
  Views = -> [View013,ProjItem031,ProjItem032]
  X = 114.304
  Y = 83.1601
  spacingX = 15
  spacingY = 15
FEATURE [TechDraw::DrawViewDimension] Dimension173
  AngleOverride = false
  Arbitrary = false
  ArbitraryTolerances = false
  BoxCorners = (2) [(-5.375,-5.375,0),(5.375,5.375,0)]
  EqualTolerance = true
  ExtensionAngle = 0
  FormatSpec = ⌀%.2w OD
  FormatSpecOverTolerance = %+.2w
  FormatSpecUnderTolerance = %+.2w
  Inverted = false
  LineAngle = 0
  LockPosition = false
  MeasureType = 1
  OverTolerance = 0
  References2D = -> [ProjItem031]
  Rotation = 0
  Scale = 0.5
  ScaleType = 0
  TheoreticalExact = false
  Type = 5
  UnderTolerance = 0
  X = 18.6033
  Y = -7.47595
FEATURE [TechDraw::DrawViewDimension] Dimension174
  AngleOverride = false
  Arbitrary = false
  ArbitraryTolerances = false
  BoxCorners = (2) [(-5.375,-62.5,-1e-07),(5.375,62.5,1e-07)]
  EqualTolerance = true
  ExtensionAngle = 0
  FormatSpec = ⌀%.2w
  FormatSpecOverTolerance = %+.2w
  FormatSpecUnderTolerance = %+.2w
  Inverted = false
  LineAngle = 0
  LockPosition = false
  MeasureType = 1
  OverTolerance = 0
  References2D = -> [View013]
  Rotation = 0
  Scale = 0.5
  ScaleType = 0
  TheoreticalExact = false
  Type = 5
  UnderTolerance = 0
  X = 16.4681
  Y = 46.8113
FEATURE [TechDraw::DrawViewDimension] Dimension176
  AngleOverride = false
  Arbitrary = false
  ArbitraryTolerances = false
  BoxCorners = (2) [(-5.375,-62.5,-1e-07),(5.375,62.5,1e-07)]
  EqualTolerance = true
  ExtensionAngle = 0
  FormatSpec = %.2w
  FormatSpecOverTolerance = %+.2w
  FormatSpecUnderTolerance = %+.2w
  Inverted = false
  LineAngle = 0
  LockPosition = false
  MeasureType = 1
  OverTolerance = 0
  References2D = -> [View013]
  Rotation = 0
  Scale = 0.5
  ScaleType = 0
  TheoreticalExact = false
  Type = 0
  UnderTolerance = 0
  X = 9.06807
  Y = 72.2351
FEATURE [TechDraw::DrawViewDimension] Dimension177
  AngleOverride = false
  Arbitrary = false
  ArbitraryTolerances = false
  BoxCorners = (2) [(-5.375,-62.5,-1e-07),(5.375,62.5,1e-07)]
  EqualTolerance = true
  ExtensionAngle = 0
  FormatSpec = %.2w
  FormatSpecOverTolerance = %+.2w
  FormatSpecUnderTolerance = %+.2w
  Inverted = false
  LineAngle = 0
  LockPosition = false
  MeasureType = 1
  OverTolerance = 0
  References2D = -> [View013]
  Rotation = 0
  Scale = 0.5
  ScaleType = 0
  TheoreticalExact = false
  Type = 2
  UnderTolerance = 0
  X = 15.4281
  Y = 55.8565
FEATURE [TechDraw::DrawViewDimension] Dimension179
  AngleOverride = false
  Arbitrary = false
  ArbitraryTolerances = false
  BoxCorners = (2) [(-5.375,-5.375,0),(5.375,5.375,0)]
  EqualTolerance = true
  ExtensionAngle = 0
  FormatSpec = ⌀%.2w ID
  FormatSpecOverTolerance = %+.2w
  FormatSpecUnderTolerance = %+.2w
  Inverted = false
  LineAngle = 0
  LockPosition = false
  MeasureType = 1
  OverTolerance = 0
  References2D = -> [ProjItem031]
  Rotation = 0
  Scale = 0.5
  ScaleType = 0
  TheoreticalExact = false
  Type = 5
  UnderTolerance = 0
  X = 16.7771
  Y = 9.59729
FEATURE [TechDraw::DrawViewDimension] Dimension180
  AngleOverride = false
  Arbitrary = false
  ArbitraryTolerances = false
  BoxCorners = (2) [(-5.375,-62.5,-1e-07),(5.375,62.5,1e-07)]
  EqualTolerance = true
  ExtensionAngle = 0
  FormatSpec = %.2w
  FormatSpecOverTolerance = %+.2w
  FormatSpecUnderTolerance = %+.2w
  Inverted = false
  LineAngle = 0
  LockPosition = false
  MeasureType = 1
  OverTolerance = 0
  References2D = -> [View013]
  Rotation = 0
  Scale = 0.5
  ScaleType = 0
  TheoreticalExact = false
  Type = 2
  UnderTolerance = 0
  X = -19.3632
  Y = 0
FEATURE [TechDraw::DrawViewAnnotation] Annotation009
  Font = osifont
  LineSpace = 100
  LockPosition = false
  MaxWidth = -1
  Rotation = 0
  Scale = 0.5
  ScaleType = 0
  Text = Note: This part is a modified metal pipe |  cut off of a broom stick. Dimentions may vary.
  TextSize = 4
  TextStyle = 0
  X = 201.03
  Y = 70.0892
FEATURE [TechDraw::DrawPage] Page012  label="HandleDrawing"
  KeepUpdated = true
  NextBalloonIndex = 1
  ProjectionType = 1
  Scale = 0.5
  Template = -> Template012
  Views = -> [ProjGroup011,Dimension173,Dimension174,Dimension176,Dimension177,Dimension179,Dimension180,Annotation009]
FEATURE [TechDraw::DrawSVGTemplate] Template013
  Height = 210
  Orientation = 1
  Template = C:/Program Files/FreeCAD 1.0/data/Mod/TechDraw/Templates/A4_Landscape_TD.svg
  Width = 297
FEATURE [TechDraw::DrawProjGroupItem] View014  label="Front012"
  CoarseView = false
  Direction = (0,-1,0)
  Focus = 100
  HardHidden = true
  IsoCount = 0
  IsoHidden = false
  IsoVisible = false
  LockPosition = true
  Perspective = false
  Rotation = 0
  RotationVector = (1,0,0)
  ScaleType = 2
  ScrubCount = 1
  SeamHidden = false
  SeamVisible = false
  SmoothHidden = false
  SmoothVisible = true
  Source = -> [Body015]
  Type = 0
  X = 0
  XDirection = (1,0,0)
  Y = 0
FEATURE [TechDraw::DrawProjGroupItem] ProjItem033  label="FrontTopRight012"
  CoarseView = false
  Direction = (0.57735,-0.57735,0.57735)
  Focus = 100
  HardHidden = false
  IsoCount = 0
  IsoHidden = false
  IsoVisible = false
  LockPosition = false
  Perspective = false
  Rotation = 0
  RotationVector = (1,0,0)
  ScaleType = 0
  ScrubCount = 1
  SeamHidden = false
  SeamVisible = false
  SmoothHidden = false
  SmoothVisible = true
  Source = -> [Body015]
  Type = 7
  X = 103.794
  XDirection = (0.707107,0.707107,0)
  Y = -3.7881
FEATURE [TechDraw::DrawProjGroupItem] ProjItem034  label="Bottom004"
  CoarseView = false
  Direction = (0,0,-1)
  Focus = 100
  HardHidden = true
  IsoCount = 0
  IsoHidden = false
  IsoVisible = false
  LockPosition = false
  Perspective = false
  Rotation = 0
  RotationVector = (1,0,0)
  ScaleType = 0
  ScrubCount = 1
  SeamHidden = false
  SeamVisible = false
  SmoothHidden = false
  SmoothVisible = true
  Source = -> [Body015]
  Type = 5
  X = 0
  XDirection = (1,0,0)
  Y = -92.1963
FEATURE [TechDraw::DrawProjGroup] ProjGroup012
  Anchor = -> View014
  AutoDistribute = false
  LockPosition = false
  ProjectionType = 1
  Rotation = 0
  ScaleType = 0
  Source = -> [Body015]
  Views = -> [View014,ProjItem033,ProjItem034]
  X = 101.528
  Y = 156.329
  spacingX = 15
  spacingY = 15
FEATURE [TechDraw::DrawViewAnnotation] Annotation010
  Font = osifont
  LineSpace = 100
  LockPosition = false
  MaxWidth = -1
  Rotation = 0
  ScaleType = 0
  Text = Note: This part is a modified PVC pipe, | dimentions may vary.
  TextSize = 4
  TextStyle = 0
  X = 196.988
  Y = 73.7482
FEATURE [TechDraw::DrawViewDimension] Dimension181
  AngleOverride = false
  Arbitrary = false
  ArbitraryTolerances = false
  BoxCorners = (2) [(-27.8,-27.7798,0),(27.8,27.7798,0)]
  EqualTolerance = true
  ExtensionAngle = 0
  FormatSpec = ⌀%.2w ID
  FormatSpecOverTolerance = %+.2w
  FormatSpecUnderTolerance = %+.2w
  Inverted = false
  LineAngle = 0
  LockPosition = false
  MeasureType = 1
  OverTolerance = 0
  References2D = -> [View014]
  Rotation = 0
  ScaleType = 0
  TheoreticalExact = false
  Type = 5
  UnderTolerance = 0
  X = -38.4492
  Y = -18.5617
FEATURE [TechDraw::DrawViewDimension] Dimension182
  AngleOverride = false
  Arbitrary = false
  ArbitraryTolerances = false
  BoxCorners = (2) [(-27.8,-27.7798,0),(27.8,27.7798,0)]
  EqualTolerance = true
  ExtensionAngle = 0
  FormatSpec = ⌀%.2w OD
  FormatSpecOverTolerance = %+.2w
  FormatSpecUnderTolerance = %+.2w
  Inverted = false
  LineAngle = 0
  LockPosition = false
  MeasureType = 1
  OverTolerance = 0
  References2D = -> [View014]
  Rotation = 0
  ScaleType = 0
  TheoreticalExact = false
  Type = 5
  UnderTolerance = 0
  X = -36.5551
  Y = 31.6306
FEATURE [TechDraw::DrawViewDimension] Dimension184
  AngleOverride = false
  Arbitrary = false
  ArbitraryTolerances = false
  BoxCorners = (2) [(-27.8,-45,-1e-07),(27.8,45,1e-07)]
  EqualTolerance = true
  ExtensionAngle = 0
  FormatSpec = %.2w
  FormatSpecOverTolerance = %+.2w
  FormatSpecUnderTolerance = %+.2w
  Inverted = false
  LineAngle = 0
  LockPosition = false
  MeasureType = 1
  OverTolerance = 0
  References2D = -> [ProjItem034]
  Rotation = 0
  ScaleType = 0
  TheoreticalExact = false
  Type = 0
  UnderTolerance = 0
  X = 37.3488
  Y = 51.7015
FEATURE [TechDraw::DrawViewDimension] Dimension185
  AngleOverride = false
  Arbitrary = false
  ArbitraryTolerances = false
  BoxCorners = (2) [(-27.8,-45,-1e-07),(27.8,45,1e-07)]
  EqualTolerance = true
  ExtensionAngle = 0
  FormatSpec = %.2w
  FormatSpecOverTolerance = %+.2w
  FormatSpecUnderTolerance = %+.2w
  Inverted = false
  LineAngle = 0
  LockPosition = false
  MeasureType = 1
  OverTolerance = 0
  References2D = -> [ProjItem034]
  Rotation = 0
  ScaleType = 0
  TheoreticalExact = false
  Type = 0
  UnderTolerance = 0
  X = 35.3732
  Y = 22.5
FEATURE [TechDraw::DrawViewDimension] Dimension186
  AngleOverride = false
  Arbitrary = false
  ArbitraryTolerances = false
  BoxCorners = (2) [(-27.8,-45,-1e-07),(27.8,45,1e-07)]
  EqualTolerance = true
  ExtensionAngle = 0
  FormatSpec = ⌀%.2w
  FormatSpecOverTolerance = %+.2w
  FormatSpecUnderTolerance = %+.2w
  Inverted = false
  LineAngle = 0
  LockPosition = false
  MeasureType = 1
  OverTolerance = 0
  References2D = -> [ProjItem034]
  Rotation = 0
  ScaleType = 0
  TheoreticalExact = false
  Type = 5
  UnderTolerance = 0
  X = -37.5746
  Y = 22.1714
FEATURE [TechDraw::DrawViewDimension] Dimension187
  AngleOverride = false
  Arbitrary = false
  ArbitraryTolerances = false
  BoxCorners = (2) [(-27.8,-27.7798,0),(27.8,27.7798,0)]
  EqualTolerance = true
  ExtensionAngle = 0
  FormatSpec = %.2w
  FormatSpecOverTolerance = %+.2w
  FormatSpecUnderTolerance = %+.2w
  Inverted = false
  LineAngle = 0
  LockPosition = false
  MeasureType = 1
  OverTolerance = 0
  References2D = -> [View014]
  Rotation = 0
  ScaleType = 0
  TheoreticalExact = false
  Type = 0
  UnderTolerance = 0
  X = -8.39156
  Y = -30.8521
FEATURE [TechDraw::DrawPage] Page013  label="ShellDrawing"
  KeepUpdated = true
  NextBalloonIndex = 1
  ProjectionType = 1
  Template = -> Template013
  Views = -> [ProjGroup012,Annotation010,Dimension181,Dimension182,Dimension184,Dimension185,Dimension186,Dimension187]
FEATURE [PartDesign::Chamfer] Chamfer
  Angle = 45
  Base = -> Chamfer003 [Edge53]
  BaseFeature = -> Chamfer003
  ChamferType = 0
  FlipDirection = false
  Refine = true
  Size = 2
  Size2 = 1
  SupportTransform = false
  Suppressed = false
  UseAllEdges = false
FEATURE [PartDesign::Body] Body007  label="Spring_Unit"
  AllowCompound = false
  Group = -> [Sketch011,Pad007,Sketch012,Pad008,PolarPattern001,Sketch013,Pad009,Sketch014,Pocket003,Chamfer003,Chamfer]
  Origin = -> Origin009
  Tip = -> Chamfer
FEATURE [App::DocumentObjectGroup] Group003  label="HammerParts"
  Group = -> [Body007,Body008,Body009,Body010,Body011,Body012,Body015,Body016,Body017,Body018,Body]
FEATURE [TechDraw::DrawProjGroupItem] ProjItem019  label="Top004"
  CoarseView = false
  Direction = (0,0,1)
  Focus = 100
  HardHidden = true
  IsoCount = 0
  IsoHidden = false
  IsoVisible = false
  LockPosition = false
  Perspective = false
  Rotation = 0
  RotationVector = (1,0,0)
  ScaleType = 2
  ScrubCount = 1
  SeamHidden = false
  SeamVisible = false
  SmoothHidden = false
  SmoothVisible = true
  Source = -> [Body007]
  Type = 4
  X = 0
  XDirection = (1,0,0)
  Y = 80.5656
FEATURE [TechDraw::DrawViewDimension] Dimension120
  AngleOverride = false
  Arbitrary = false
  ArbitraryTolerances = false
  BoxCorners = (2) [(-34.65,-34.65,0),(34.65,34.65,0)]
  EqualTolerance = true
  ExtensionAngle = 0
  FormatSpec = %.2w x45°
  FormatSpecOverTolerance = %+.2w
  FormatSpecUnderTolerance = %+.2w
  Inverted = false
  LineAngle = 0
  LockPosition = false
  MeasureType = 1
  OverTolerance = 0
  References2D = -> [ProjItem019]
  Rotation = 0
  Scale = 3
  ScaleType = 0
  TheoreticalExact = false
  Type = 2
  UnderTolerance = 0
  X = 44.3017
  Y = 33.15
FEATURE [TechDraw::DrawViewDimension] Dimension121
  AngleOverride = false
  Arbitrary = false
  ArbitraryTolerances = false
  BoxCorners = (2) [(-34.65,-34.65,0),(34.65,34.65,0)]
  EqualTolerance = true
  ExtensionAngle = 0
  FormatSpec = %.2w x45°
  FormatSpecOverTolerance = %+.2w
  FormatSpecUnderTolerance = %+.2w
  Inverted = false
  LineAngle = 0
  LockPosition = false
  MeasureType = 1
  OverTolerance = 0
  References2D = -> [ProjItem019]
  Rotation = 0
  Scale = 3
  ScaleType = 0
  TheoreticalExact = false
  Type = 1
  UnderTolerance = 0
  X = 33.15
  Y = 44.6805
FEATURE [TechDraw::DrawViewDimension] Dimension122
  AngleOverride = false
  Arbitrary = false
  ArbitraryTolerances = false
  BoxCorners = (2) [(-34.65,-34.65,0),(34.65,34.65,0)]
  EqualTolerance = true
  ExtensionAngle = 0
  FormatSpec = %.2w
  FormatSpecOverTolerance = %+.2w
  FormatSpecUnderTolerance = %+.2w
  Inverted = false
  LineAngle = 0
  LockPosition = false
  MeasureType = 1
  OverTolerance = 0
  References2D = -> [ProjItem019]
  Rotation = 0
  Scale = 3
  ScaleType = 0
  TheoreticalExact = false
  Type = 1
  UnderTolerance = 0
  X = 0
  Y = -42.1486
FEATURE [TechDraw::DrawViewDimension] Dimension123
  AngleOverride = false
  Arbitrary = false
  ArbitraryTolerances = false
  BoxCorners = (2) [(-34.65,-34.65,0),(34.65,34.65,0)]
  EqualTolerance = true
  ExtensionAngle = 0
  FormatSpec = %.2w
  FormatSpecOverTolerance = %+.2w
  FormatSpecUnderTolerance = %+.2w
  Inverted = false
  LineAngle = 0
  LockPosition = false
  MeasureType = 1
  OverTolerance = 0
  References2D = -> [ProjItem019]
  Rotation = 0
  Scale = 3
  ScaleType = 0
  TheoreticalExact = false
  Type = 2
  UnderTolerance = 0
  X = -45.2807
  Y = 0
FEATURE [TechDraw::DrawViewDimension] Dimension124
  AngleOverride = false
  Arbitrary = false
  ArbitraryTolerances = false
  BoxCorners = (2) [(-34.65,-34.65,0),(34.65,34.65,0)]
  EqualTolerance = true
  ExtensionAngle = 0
  FormatSpec = ⌀%.2w↧10
  FormatSpecOverTolerance = %+.2w
  FormatSpecUnderTolerance = %+.2w
  Inverted = false
  LineAngle = 0
  LockPosition = false
  MeasureType = 1
  OverTolerance = 0
  References2D = -> [ProjItem019]
  Rotation = 0
  Scale = 3
  ScaleType = 0
  TheoreticalExact = false
  Type = 5
  UnderTolerance = 0
  X = 45.7307
  Y = -15.992
FEATURE [TechDraw::DrawProjGroupItem] ProjItem020  label="FrontTopRight007"
  CoarseView = false
  Direction = (0.57735,-0.57735,0.57735)
  Focus = 100
  HardHidden = false
  IsoCount = 0
  IsoHidden = false
  IsoVisible = false
  LockPosition = false
  Perspective = false
  Rotation = 0
  RotationVector = (1,0,0)
  ScaleType = 2
  ScrubCount = 1
  SeamHidden = false
  SeamVisible = false
  SmoothHidden = false
  SmoothVisible = true
  Source = -> [Body007]
  Type = 7
  X = 116.488
  XDirection = (0.707107,0.707107,0)
  Y = 79.805
FEATURE [TechDraw::DrawProjGroupItem] View008  label="Front007"
  CoarseView = false
  Direction = (0,-1,0)
  Focus = 100
  HardHidden = true
  IsoCount = 0
  IsoHidden = false
  IsoVisible = false
  LockPosition = true
  Perspective = false
  Rotation = 0
  RotationVector = (1,0,0)
  Scale = 3
  ScaleType = 2
  ScrubCount = 1
  SeamHidden = false
  SeamVisible = false
  SmoothHidden = false
  SmoothVisible = true
  Source = -> [Body007]
  Type = 0
  X = 0
  XDirection = (1,0,0)
  Y = 0
FEATURE [TechDraw::DrawViewDimension] Dimension125
  AngleOverride = false
  Arbitrary = false
  ArbitraryTolerances = false
  BoxCorners = (2) [(-34.65,-21,-1e-07),(34.65,21,1e-07)]
  EqualTolerance = true
  ExtensionAngle = 0
  FormatSpec = %.2w
  FormatSpecOverTolerance = %+.2w
  FormatSpecUnderTolerance = %+.2w
  Inverted = false
  LineAngle = 0
  LockPosition = false
  MeasureType = 1
  OverTolerance = 0
  References2D = -> [View008]
  Rotation = 0
  Scale = 3
  ScaleType = 0
  TheoreticalExact = false
  Type = 2
  UnderTolerance = 0
  X = -61.7542
  Y = 0
FEATURE [TechDraw::DrawViewDimension] Dimension126
  AngleOverride = false
  Arbitrary = false
  ArbitraryTolerances = false
  BoxCorners = (2) [(-34.65,-21,-1e-07),(34.65,21,1e-07)]
  EqualTolerance = true
  ExtensionAngle = 0
  FormatSpec = %.2w
  FormatSpecOverTolerance = %+.2w
  FormatSpecUnderTolerance = %+.2w
  Inverted = false
  LineAngle = 0
  LockPosition = false
  MeasureType = 1
  OverTolerance = 0
  References2D = -> [View008]
  Rotation = 0
  Scale = 3
  ScaleType = 0
  TheoreticalExact = false
  Type = 2
  UnderTolerance = 0
  X = -51.5734
  Y = 9.3
FEATURE [TechDraw::DrawViewDimension] Dimension127
  AngleOverride = false
  Arbitrary = false
  ArbitraryTolerances = false
  BoxCorners = (2) [(-34.65,-21,-1e-07),(34.65,21,1e-07)]
  EqualTolerance = true
  ExtensionAngle = 0
  FormatSpec = %.2w
  FormatSpecOverTolerance = %+.2w
  FormatSpecUnderTolerance = %+.2w
  Inverted = false
  LineAngle = 0
  LockPosition = false
  MeasureType = 1
  OverTolerance = 0
  References2D = -> [View008]
  Rotation = 0
  Scale = 3
  ScaleType = 0
  TheoreticalExact = false
  Type = 2
  UnderTolerance = 0
  X = -42.2485
  Y = 13.5
FEATURE [TechDraw::DrawViewDimension] Dimension128
  AngleOverride = false
  Arbitrary = false
  ArbitraryTolerances = false
  BoxCorners = (2) [(-34.65,-21,-1e-07),(34.65,21,1e-07)]
  EqualTolerance = true
  ExtensionAngle = 0
  FormatSpec = %.2w
  FormatSpecOverTolerance = %+.2w
  FormatSpecUnderTolerance = %+.2w
  Inverted = false
  LineAngle = 0
  LockPosition = false
  MeasureType = 1
  OverTolerance = 0
  References2D = -> [View008]
  Rotation = 0
  Scale = 3
  ScaleType = 0
  TheoreticalExact = false
  Type = 1
  UnderTolerance = 0
  X = 0
  Y = -26.841
FEATURE [TechDraw::DrawViewDimension] Dimension129
  AngleOverride = false
  Arbitrary = false
  ArbitraryTolerances = false
  BoxCorners = (2) [(-34.65,-21,-1e-07),(34.65,21,1e-07)]
  EqualTolerance = true
  ExtensionAngle = 0
  FormatSpec = %.2w
  FormatSpecOverTolerance = %+.2w
  FormatSpecUnderTolerance = %+.2w
  Inverted = false
  LineAngle = 0
  LockPosition = false
  MeasureType = 1
  OverTolerance = 0
  References2D = -> [View008]
  Rotation = 0
  Scale = 3
  ScaleType = 0
  TheoreticalExact = false
  Type = 6
  UnderTolerance = 0
  X = 43.3483
  Y = -0.230837
FEATURE [TechDraw::DrawProjGroup] ProjGroup007
  Anchor = -> View008
  AutoDistribute = false
  LockPosition = false
  ProjectionType = 1
  Rotation = 0
  Scale = 3
  ScaleType = 0
  Source = -> [Body007]
  Views = -> [View008,ProjItem019,ProjItem020]
  X = 94.897
  Y = 61.1804
  spacingX = 15
  spacingY = 15
FEATURE [TechDraw::DrawPage] Page007  label="Pusher_Drawing"
  KeepUpdated = true
  NextBalloonIndex = 1
  ProjectionType = 1
  Scale = 3
  Template = -> Template007
  Views = -> [ProjGroup007,Dimension120,Dimension121,Dimension122,Dimension123,Dimension124,Dimension125,Dimension126,Dimension127,Dimension128,Dimension129,Annotation007]
FEATURE [App::DocumentObjectGroup] Group  label="Drawings"
  Group = -> [Page007,Page008,Page009,Page010,Page006,Page011,Page012,Page,Group005,Page013]
note: 2 file-system paths scrubbed to <path> (originals preserved in the JSON sidecar)
